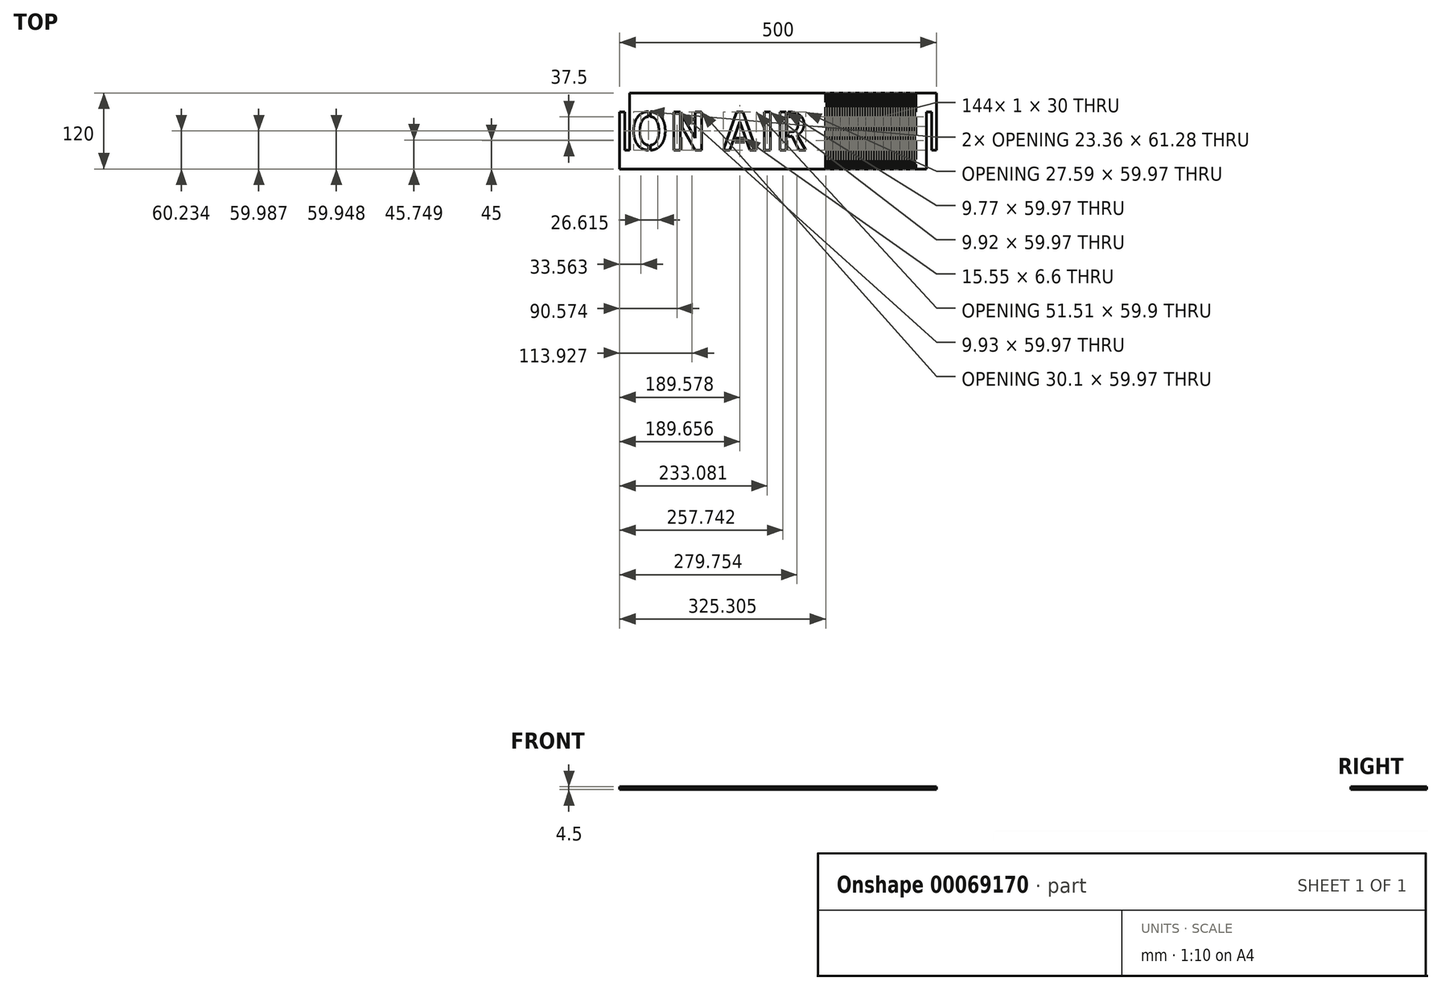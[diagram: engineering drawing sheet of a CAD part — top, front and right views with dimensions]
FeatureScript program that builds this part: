
annotation { "Feature Type Name" : "Feature", "Feature Type Description" : "" }
export const myFeature = defineFeature(function(context is Context, id is Id, definition is map)
    precondition{}
    {
        {
            var Q0;
            Q0=qCreatedBy(makeId("Top.planeOp"),FACE);
            var sketch = newSketch(context, id + "F0", { "sketchPlane" : qUnion([Q0])});
            skLineSegment(sketch, "E0", {"start": v(0, 0) * mm, "end": v(484.38, 0) * mm});
            skLineSegment(sketch, "E1", {"start": v(484.38, 0) * mm, "end": v(484.38, 90) * mm});
            skLineSegment(sketch, "E2", {"start": v(484.38, 90) * mm, "end": v(492.19, 90) * mm});
            skLineSegment(sketch, "E3", {"start": v(492.19, 90) * mm, "end": v(492.19, 30) * mm});
            skLineSegment(sketch, "E4", {"start": v(500, 30) * mm, "end": v(500, 120) * mm});
            skLineSegment(sketch, "E5", {"start": v(500, 120) * mm, "end": v(15.62, 120) * mm});
            skLineSegment(sketch, "E6", {"start": v(0, 90) * mm, "end": v(0, 0) * mm});
            skText(sketch, "E7", { "text": "ON AIR", "fontName": "AllertaStencil-Regular.ttf"});
            skLineSegment(sketch, "E8", {"start": v(7.81, 90) * mm, "end": v(7.81, 30) * mm});
            skLineSegment(sketch, "E9", {"start": v(7.81, 30) * mm, "end": v(15.62, 30) * mm});
            skLineSegment(sketch, "E10", {"start": v(15.62, 30) * mm, "end": v(15.62, 120) * mm});
            skLineSegment(sketch, "E11", {"start": v(0, 90) * mm, "end": v(7.81, 90) * mm});
            skLineSegment(sketch, "E12", {"start": v(492.19, 30) * mm, "end": v(500, 30) * mm});
            skLineSegment(sketch, "E13", {"start": v(324.8, 135) * mm, "end": v(324.8, 105) * mm});
            skLineSegment(sketch, "E14", {"start": v(324.8, 105) * mm, "end": v(325.8, 105) * mm});
            skLineSegment(sketch, "E15", {"start": v(325.8, 105) * mm, "end": v(325.8, 135) * mm});
            skLineSegment(sketch, "E16", {"start": v(325.8, 135) * mm, "end": v(324.8, 135) * mm});
            skPoint(sketch, "E17", {"position": v(324.8, 120) * mm});
            skLineSegment(sketch, "E18", {"start": v(326.8, 120) * mm, "end": v(326.8, 90) * mm});
            skLineSegment(sketch, "E19", {"start": v(326.8, 90) * mm, "end": v(327.8, 90) * mm});
            skLineSegment(sketch, "E20", {"start": v(327.8, 90) * mm, "end": v(327.8, 120) * mm});
            skLineSegment(sketch, "E21", {"start": v(327.8, 120) * mm, "end": v(326.8, 120) * mm});
            skLineSegment(sketch, "E22.0.1.0", {"start": v(327.8, 52.5) * mm, "end": v(327.8, 82.5) * mm});
            skLineSegment(sketch, "E22.0.1.1", {"start": v(324.8, 97.5) * mm, "end": v(324.8, 67.5) * mm});
            skPoint(sketch, "E22.0.1.2", {"position": v(324.8, 82.5) * mm});
            skLineSegment(sketch, "E22.0.1.3", {"start": v(325.8, 67.5) * mm, "end": v(325.8, 97.5) * mm});
            skLineSegment(sketch, "E22.0.1.4", {"start": v(326.8, 82.5) * mm, "end": v(326.8, 52.5) * mm});
            skLineSegment(sketch, "E22.0.1.5", {"start": v(324.8, 67.5) * mm, "end": v(325.8, 67.5) * mm});
            skLineSegment(sketch, "E22.0.1.6", {"start": v(327.8, 82.5) * mm, "end": v(326.8, 82.5) * mm});
            skLineSegment(sketch, "E22.0.1.7", {"start": v(325.8, 97.5) * mm, "end": v(324.8, 97.5) * mm});
            skLineSegment(sketch, "E22.0.1.8", {"start": v(326.8, 52.5) * mm, "end": v(327.8, 52.5) * mm});
            skLineSegment(sketch, "E22.0.2.0", {"start": v(327.8, 15) * mm, "end": v(327.8, 45) * mm});
            skLineSegment(sketch, "E22.0.2.1", {"start": v(324.8, 60) * mm, "end": v(324.8, 30) * mm});
            skPoint(sketch, "E22.0.2.2", {"position": v(324.8, 45) * mm});
            skLineSegment(sketch, "E22.0.2.3", {"start": v(325.8, 30) * mm, "end": v(325.8, 60) * mm});
            skLineSegment(sketch, "E22.0.2.4", {"start": v(326.8, 45) * mm, "end": v(326.8, 15) * mm});
            skLineSegment(sketch, "E22.0.2.5", {"start": v(324.8, 30) * mm, "end": v(325.8, 30) * mm});
            skLineSegment(sketch, "E22.0.2.6", {"start": v(327.8, 45) * mm, "end": v(326.8, 45) * mm});
            skLineSegment(sketch, "E22.0.2.7", {"start": v(325.8, 60) * mm, "end": v(324.8, 60) * mm});
            skLineSegment(sketch, "E22.0.2.8", {"start": v(326.8, 15) * mm, "end": v(327.8, 15) * mm});
            skLineSegment(sketch, "E22.0.3.0", {"start": v(327.8, -22.5) * mm, "end": v(327.8, 7.5) * mm});
            skLineSegment(sketch, "E22.0.3.1", {"start": v(324.8, 22.5) * mm, "end": v(324.8, -7.5) * mm});
            skPoint(sketch, "E22.0.3.2", {"position": v(324.8, 7.5) * mm});
            skLineSegment(sketch, "E22.0.3.3", {"start": v(325.8, -7.5) * mm, "end": v(325.8, 22.5) * mm});
            skLineSegment(sketch, "E22.0.3.4", {"start": v(326.8, 7.5) * mm, "end": v(326.8, -22.5) * mm});
            skLineSegment(sketch, "E22.0.3.5", {"start": v(324.8, -7.5) * mm, "end": v(325.8, -7.5) * mm});
            skLineSegment(sketch, "E22.0.3.6", {"start": v(327.8, 7.5) * mm, "end": v(326.8, 7.5) * mm});
            skLineSegment(sketch, "E22.0.3.7", {"start": v(325.8, 22.5) * mm, "end": v(324.8, 22.5) * mm});
            skLineSegment(sketch, "E22.0.3.8", {"start": v(326.8, -22.5) * mm, "end": v(327.8, -22.5) * mm});
            skLineSegment(sketch, "E22.1.0.0", {"start": v(331.8, 90) * mm, "end": v(331.8, 120) * mm});
            skLineSegment(sketch, "E22.1.0.1", {"start": v(328.8, 135) * mm, "end": v(328.8, 105) * mm});
            skPoint(sketch, "E22.1.0.2", {"position": v(328.8, 120) * mm});
            skLineSegment(sketch, "E22.1.0.3", {"start": v(329.8, 105) * mm, "end": v(329.8, 135) * mm});
            skLineSegment(sketch, "E22.1.0.4", {"start": v(330.8, 120) * mm, "end": v(330.8, 90) * mm});
            skLineSegment(sketch, "E22.1.0.5", {"start": v(328.8, 105) * mm, "end": v(329.8, 105) * mm});
            skLineSegment(sketch, "E22.1.0.6", {"start": v(331.8, 120) * mm, "end": v(330.8, 120) * mm});
            skLineSegment(sketch, "E22.1.0.7", {"start": v(329.8, 135) * mm, "end": v(328.8, 135) * mm});
            skLineSegment(sketch, "E22.1.0.8", {"start": v(330.8, 90) * mm, "end": v(331.8, 90) * mm});
            skLineSegment(sketch, "E22.1.1.0", {"start": v(331.8, 52.5) * mm, "end": v(331.8, 82.5) * mm});
            skLineSegment(sketch, "E22.1.1.1", {"start": v(328.8, 97.5) * mm, "end": v(328.8, 67.5) * mm});
            skPoint(sketch, "E22.1.1.2", {"position": v(328.8, 82.5) * mm});
            skLineSegment(sketch, "E22.1.1.3", {"start": v(329.8, 67.5) * mm, "end": v(329.8, 97.5) * mm});
            skLineSegment(sketch, "E22.1.1.4", {"start": v(330.8, 82.5) * mm, "end": v(330.8, 52.5) * mm});
            skLineSegment(sketch, "E22.1.1.5", {"start": v(328.8, 67.5) * mm, "end": v(329.8, 67.5) * mm});
            skLineSegment(sketch, "E22.1.1.6", {"start": v(331.8, 82.5) * mm, "end": v(330.8, 82.5) * mm});
            skLineSegment(sketch, "E22.1.1.7", {"start": v(329.8, 97.5) * mm, "end": v(328.8, 97.5) * mm});
            skLineSegment(sketch, "E22.1.1.8", {"start": v(330.8, 52.5) * mm, "end": v(331.8, 52.5) * mm});
            skLineSegment(sketch, "E22.1.2.0", {"start": v(331.8, 15) * mm, "end": v(331.8, 45) * mm});
            skLineSegment(sketch, "E22.1.2.1", {"start": v(328.8, 60) * mm, "end": v(328.8, 30) * mm});
            skPoint(sketch, "E22.1.2.2", {"position": v(328.8, 45) * mm});
            skLineSegment(sketch, "E22.1.2.3", {"start": v(329.8, 30) * mm, "end": v(329.8, 60) * mm});
            skLineSegment(sketch, "E22.1.2.4", {"start": v(330.8, 45) * mm, "end": v(330.8, 15) * mm});
            skLineSegment(sketch, "E22.1.2.5", {"start": v(328.8, 30) * mm, "end": v(329.8, 30) * mm});
            skLineSegment(sketch, "E22.1.2.6", {"start": v(331.8, 45) * mm, "end": v(330.8, 45) * mm});
            skLineSegment(sketch, "E22.1.2.7", {"start": v(329.8, 60) * mm, "end": v(328.8, 60) * mm});
            skLineSegment(sketch, "E22.1.2.8", {"start": v(330.8, 15) * mm, "end": v(331.8, 15) * mm});
            skLineSegment(sketch, "E22.1.3.0", {"start": v(331.8, -22.5) * mm, "end": v(331.8, 7.5) * mm});
            skLineSegment(sketch, "E22.1.3.1", {"start": v(328.8, 22.5) * mm, "end": v(328.8, -7.5) * mm});
            skPoint(sketch, "E22.1.3.2", {"position": v(328.8, 7.5) * mm});
            skLineSegment(sketch, "E22.1.3.3", {"start": v(329.8, -7.5) * mm, "end": v(329.8, 22.5) * mm});
            skLineSegment(sketch, "E22.1.3.4", {"start": v(330.8, 7.5) * mm, "end": v(330.8, -22.5) * mm});
            skLineSegment(sketch, "E22.1.3.5", {"start": v(328.8, -7.5) * mm, "end": v(329.8, -7.5) * mm});
            skLineSegment(sketch, "E22.1.3.6", {"start": v(331.8, 7.5) * mm, "end": v(330.8, 7.5) * mm});
            skLineSegment(sketch, "E22.1.3.7", {"start": v(329.8, 22.5) * mm, "end": v(328.8, 22.5) * mm});
            skLineSegment(sketch, "E22.1.3.8", {"start": v(330.8, -22.5) * mm, "end": v(331.8, -22.5) * mm});
            skLineSegment(sketch, "E22.2.0.0", {"start": v(335.8, 90) * mm, "end": v(335.8, 120) * mm});
            skLineSegment(sketch, "E22.2.0.1", {"start": v(332.8, 135) * mm, "end": v(332.8, 105) * mm});
            skPoint(sketch, "E22.2.0.2", {"position": v(332.8, 120) * mm});
            skLineSegment(sketch, "E22.2.0.3", {"start": v(333.8, 105) * mm, "end": v(333.8, 135) * mm});
            skLineSegment(sketch, "E22.2.0.4", {"start": v(334.8, 120) * mm, "end": v(334.8, 90) * mm});
            skLineSegment(sketch, "E22.2.0.5", {"start": v(332.8, 105) * mm, "end": v(333.8, 105) * mm});
            skLineSegment(sketch, "E22.2.0.6", {"start": v(335.8, 120) * mm, "end": v(334.8, 120) * mm});
            skLineSegment(sketch, "E22.2.0.7", {"start": v(333.8, 135) * mm, "end": v(332.8, 135) * mm});
            skLineSegment(sketch, "E22.2.0.8", {"start": v(334.8, 90) * mm, "end": v(335.8, 90) * mm});
            skLineSegment(sketch, "E22.2.1.0", {"start": v(335.8, 52.5) * mm, "end": v(335.8, 82.5) * mm});
            skLineSegment(sketch, "E22.2.1.1", {"start": v(332.8, 97.5) * mm, "end": v(332.8, 67.5) * mm});
            skPoint(sketch, "E22.2.1.2", {"position": v(332.8, 82.5) * mm});
            skLineSegment(sketch, "E22.2.1.3", {"start": v(333.8, 67.5) * mm, "end": v(333.8, 97.5) * mm});
            skLineSegment(sketch, "E22.2.1.4", {"start": v(334.8, 82.5) * mm, "end": v(334.8, 52.5) * mm});
            skLineSegment(sketch, "E22.2.1.5", {"start": v(332.8, 67.5) * mm, "end": v(333.8, 67.5) * mm});
            skLineSegment(sketch, "E22.2.1.6", {"start": v(335.8, 82.5) * mm, "end": v(334.8, 82.5) * mm});
            skLineSegment(sketch, "E22.2.1.7", {"start": v(333.8, 97.5) * mm, "end": v(332.8, 97.5) * mm});
            skLineSegment(sketch, "E22.2.1.8", {"start": v(334.8, 52.5) * mm, "end": v(335.8, 52.5) * mm});
            skLineSegment(sketch, "E22.2.2.0", {"start": v(335.8, 15) * mm, "end": v(335.8, 45) * mm});
            skLineSegment(sketch, "E22.2.2.1", {"start": v(332.8, 60) * mm, "end": v(332.8, 30) * mm});
            skPoint(sketch, "E22.2.2.2", {"position": v(332.8, 45) * mm});
            skLineSegment(sketch, "E22.2.2.3", {"start": v(333.8, 30) * mm, "end": v(333.8, 60) * mm});
            skLineSegment(sketch, "E22.2.2.4", {"start": v(334.8, 45) * mm, "end": v(334.8, 15) * mm});
            skLineSegment(sketch, "E22.2.2.5", {"start": v(332.8, 30) * mm, "end": v(333.8, 30) * mm});
            skLineSegment(sketch, "E22.2.2.6", {"start": v(335.8, 45) * mm, "end": v(334.8, 45) * mm});
            skLineSegment(sketch, "E22.2.2.7", {"start": v(333.8, 60) * mm, "end": v(332.8, 60) * mm});
            skLineSegment(sketch, "E22.2.2.8", {"start": v(334.8, 15) * mm, "end": v(335.8, 15) * mm});
            skLineSegment(sketch, "E22.2.3.0", {"start": v(335.8, -22.5) * mm, "end": v(335.8, 7.5) * mm});
            skLineSegment(sketch, "E22.2.3.1", {"start": v(332.8, 22.5) * mm, "end": v(332.8, -7.5) * mm});
            skPoint(sketch, "E22.2.3.2", {"position": v(332.8, 7.5) * mm});
            skLineSegment(sketch, "E22.2.3.3", {"start": v(333.8, -7.5) * mm, "end": v(333.8, 22.5) * mm});
            skLineSegment(sketch, "E22.2.3.4", {"start": v(334.8, 7.5) * mm, "end": v(334.8, -22.5) * mm});
            skLineSegment(sketch, "E22.2.3.5", {"start": v(332.8, -7.5) * mm, "end": v(333.8, -7.5) * mm});
            skLineSegment(sketch, "E22.2.3.6", {"start": v(335.8, 7.5) * mm, "end": v(334.8, 7.5) * mm});
            skLineSegment(sketch, "E22.2.3.7", {"start": v(333.8, 22.5) * mm, "end": v(332.8, 22.5) * mm});
            skLineSegment(sketch, "E22.2.3.8", {"start": v(334.8, -22.5) * mm, "end": v(335.8, -22.5) * mm});
            skLineSegment(sketch, "E22.3.0.0", {"start": v(339.8, 90) * mm, "end": v(339.8, 120) * mm});
            skLineSegment(sketch, "E22.3.0.1", {"start": v(336.8, 135) * mm, "end": v(336.8, 105) * mm});
            skPoint(sketch, "E22.3.0.2", {"position": v(336.8, 120) * mm});
            skLineSegment(sketch, "E22.3.0.3", {"start": v(337.8, 105) * mm, "end": v(337.8, 135) * mm});
            skLineSegment(sketch, "E22.3.0.4", {"start": v(338.8, 120) * mm, "end": v(338.8, 90) * mm});
            skLineSegment(sketch, "E22.3.0.5", {"start": v(336.8, 105) * mm, "end": v(337.8, 105) * mm});
            skLineSegment(sketch, "E22.3.0.6", {"start": v(339.8, 120) * mm, "end": v(338.8, 120) * mm});
            skLineSegment(sketch, "E22.3.0.7", {"start": v(337.8, 135) * mm, "end": v(336.8, 135) * mm});
            skLineSegment(sketch, "E22.3.0.8", {"start": v(338.8, 90) * mm, "end": v(339.8, 90) * mm});
            skLineSegment(sketch, "E22.3.1.0", {"start": v(339.8, 52.5) * mm, "end": v(339.8, 82.5) * mm});
            skLineSegment(sketch, "E22.3.1.1", {"start": v(336.8, 97.5) * mm, "end": v(336.8, 67.5) * mm});
            skPoint(sketch, "E22.3.1.2", {"position": v(336.8, 82.5) * mm});
            skLineSegment(sketch, "E22.3.1.3", {"start": v(337.8, 67.5) * mm, "end": v(337.8, 97.5) * mm});
            skLineSegment(sketch, "E22.3.1.4", {"start": v(338.8, 82.5) * mm, "end": v(338.8, 52.5) * mm});
            skLineSegment(sketch, "E22.3.1.5", {"start": v(336.8, 67.5) * mm, "end": v(337.8, 67.5) * mm});
            skLineSegment(sketch, "E22.3.1.6", {"start": v(339.8, 82.5) * mm, "end": v(338.8, 82.5) * mm});
            skLineSegment(sketch, "E22.3.1.7", {"start": v(337.8, 97.5) * mm, "end": v(336.8, 97.5) * mm});
            skLineSegment(sketch, "E22.3.1.8", {"start": v(338.8, 52.5) * mm, "end": v(339.8, 52.5) * mm});
            skLineSegment(sketch, "E22.3.2.0", {"start": v(339.8, 15) * mm, "end": v(339.8, 45) * mm});
            skLineSegment(sketch, "E22.3.2.1", {"start": v(336.8, 60) * mm, "end": v(336.8, 30) * mm});
            skPoint(sketch, "E22.3.2.2", {"position": v(336.8, 45) * mm});
            skLineSegment(sketch, "E22.3.2.3", {"start": v(337.8, 30) * mm, "end": v(337.8, 60) * mm});
            skLineSegment(sketch, "E22.3.2.4", {"start": v(338.8, 45) * mm, "end": v(338.8, 15) * mm});
            skLineSegment(sketch, "E22.3.2.5", {"start": v(336.8, 30) * mm, "end": v(337.8, 30) * mm});
            skLineSegment(sketch, "E22.3.2.6", {"start": v(339.8, 45) * mm, "end": v(338.8, 45) * mm});
            skLineSegment(sketch, "E22.3.2.7", {"start": v(337.8, 60) * mm, "end": v(336.8, 60) * mm});
            skLineSegment(sketch, "E22.3.2.8", {"start": v(338.8, 15) * mm, "end": v(339.8, 15) * mm});
            skLineSegment(sketch, "E22.3.3.0", {"start": v(339.8, -22.5) * mm, "end": v(339.8, 7.5) * mm});
            skLineSegment(sketch, "E22.3.3.1", {"start": v(336.8, 22.5) * mm, "end": v(336.8, -7.5) * mm});
            skPoint(sketch, "E22.3.3.2", {"position": v(336.8, 7.5) * mm});
            skLineSegment(sketch, "E22.3.3.3", {"start": v(337.8, -7.5) * mm, "end": v(337.8, 22.5) * mm});
            skLineSegment(sketch, "E22.3.3.4", {"start": v(338.8, 7.5) * mm, "end": v(338.8, -22.5) * mm});
            skLineSegment(sketch, "E22.3.3.5", {"start": v(336.8, -7.5) * mm, "end": v(337.8, -7.5) * mm});
            skLineSegment(sketch, "E22.3.3.6", {"start": v(339.8, 7.5) * mm, "end": v(338.8, 7.5) * mm});
            skLineSegment(sketch, "E22.3.3.7", {"start": v(337.8, 22.5) * mm, "end": v(336.8, 22.5) * mm});
            skLineSegment(sketch, "E22.3.3.8", {"start": v(338.8, -22.5) * mm, "end": v(339.8, -22.5) * mm});
            skLineSegment(sketch, "E22.4.0.0", {"start": v(343.8, 90) * mm, "end": v(343.8, 120) * mm});
            skLineSegment(sketch, "E22.4.0.1", {"start": v(340.8, 135) * mm, "end": v(340.8, 105) * mm});
            skPoint(sketch, "E22.4.0.2", {"position": v(340.8, 120) * mm});
            skLineSegment(sketch, "E22.4.0.3", {"start": v(341.8, 105) * mm, "end": v(341.8, 135) * mm});
            skLineSegment(sketch, "E22.4.0.4", {"start": v(342.8, 120) * mm, "end": v(342.8, 90) * mm});
            skLineSegment(sketch, "E22.4.0.5", {"start": v(340.8, 105) * mm, "end": v(341.8, 105) * mm});
            skLineSegment(sketch, "E22.4.0.6", {"start": v(343.8, 120) * mm, "end": v(342.8, 120) * mm});
            skLineSegment(sketch, "E22.4.0.7", {"start": v(341.8, 135) * mm, "end": v(340.8, 135) * mm});
            skLineSegment(sketch, "E22.4.0.8", {"start": v(342.8, 90) * mm, "end": v(343.8, 90) * mm});
            skLineSegment(sketch, "E22.4.1.0", {"start": v(343.8, 52.5) * mm, "end": v(343.8, 82.5) * mm});
            skLineSegment(sketch, "E22.4.1.1", {"start": v(340.8, 97.5) * mm, "end": v(340.8, 67.5) * mm});
            skPoint(sketch, "E22.4.1.2", {"position": v(340.8, 82.5) * mm});
            skLineSegment(sketch, "E22.4.1.3", {"start": v(341.8, 67.5) * mm, "end": v(341.8, 97.5) * mm});
            skLineSegment(sketch, "E22.4.1.4", {"start": v(342.8, 82.5) * mm, "end": v(342.8, 52.5) * mm});
            skLineSegment(sketch, "E22.4.1.5", {"start": v(340.8, 67.5) * mm, "end": v(341.8, 67.5) * mm});
            skLineSegment(sketch, "E22.4.1.6", {"start": v(343.8, 82.5) * mm, "end": v(342.8, 82.5) * mm});
            skLineSegment(sketch, "E22.4.1.7", {"start": v(341.8, 97.5) * mm, "end": v(340.8, 97.5) * mm});
            skLineSegment(sketch, "E22.4.1.8", {"start": v(342.8, 52.5) * mm, "end": v(343.8, 52.5) * mm});
            skLineSegment(sketch, "E22.4.2.0", {"start": v(343.8, 15) * mm, "end": v(343.8, 45) * mm});
            skLineSegment(sketch, "E22.4.2.1", {"start": v(340.8, 60) * mm, "end": v(340.8, 30) * mm});
            skPoint(sketch, "E22.4.2.2", {"position": v(340.8, 45) * mm});
            skLineSegment(sketch, "E22.4.2.3", {"start": v(341.8, 30) * mm, "end": v(341.8, 60) * mm});
            skLineSegment(sketch, "E22.4.2.4", {"start": v(342.8, 45) * mm, "end": v(342.8, 15) * mm});
            skLineSegment(sketch, "E22.4.2.5", {"start": v(340.8, 30) * mm, "end": v(341.8, 30) * mm});
            skLineSegment(sketch, "E22.4.2.6", {"start": v(343.8, 45) * mm, "end": v(342.8, 45) * mm});
            skLineSegment(sketch, "E22.4.2.7", {"start": v(341.8, 60) * mm, "end": v(340.8, 60) * mm});
            skLineSegment(sketch, "E22.4.2.8", {"start": v(342.8, 15) * mm, "end": v(343.8, 15) * mm});
            skLineSegment(sketch, "E22.4.3.0", {"start": v(343.8, -22.5) * mm, "end": v(343.8, 7.5) * mm});
            skLineSegment(sketch, "E22.4.3.1", {"start": v(340.8, 22.5) * mm, "end": v(340.8, -7.5) * mm});
            skPoint(sketch, "E22.4.3.2", {"position": v(340.8, 7.5) * mm});
            skLineSegment(sketch, "E22.4.3.3", {"start": v(341.8, -7.5) * mm, "end": v(341.8, 22.5) * mm});
            skLineSegment(sketch, "E22.4.3.4", {"start": v(342.8, 7.5) * mm, "end": v(342.8, -22.5) * mm});
            skLineSegment(sketch, "E22.4.3.5", {"start": v(340.8, -7.5) * mm, "end": v(341.8, -7.5) * mm});
            skLineSegment(sketch, "E22.4.3.6", {"start": v(343.8, 7.5) * mm, "end": v(342.8, 7.5) * mm});
            skLineSegment(sketch, "E22.4.3.7", {"start": v(341.8, 22.5) * mm, "end": v(340.8, 22.5) * mm});
            skLineSegment(sketch, "E22.4.3.8", {"start": v(342.8, -22.5) * mm, "end": v(343.8, -22.5) * mm});
            skLineSegment(sketch, "E22.5.0.0", {"start": v(347.8, 90) * mm, "end": v(347.8, 120) * mm});
            skLineSegment(sketch, "E22.5.0.1", {"start": v(344.8, 135) * mm, "end": v(344.8, 105) * mm});
            skPoint(sketch, "E22.5.0.2", {"position": v(344.8, 120) * mm});
            skLineSegment(sketch, "E22.5.0.3", {"start": v(345.8, 105) * mm, "end": v(345.8, 135) * mm});
            skLineSegment(sketch, "E22.5.0.4", {"start": v(346.8, 120) * mm, "end": v(346.8, 90) * mm});
            skLineSegment(sketch, "E22.5.0.5", {"start": v(344.8, 105) * mm, "end": v(345.8, 105) * mm});
            skLineSegment(sketch, "E22.5.0.6", {"start": v(347.8, 120) * mm, "end": v(346.8, 120) * mm});
            skLineSegment(sketch, "E22.5.0.7", {"start": v(345.8, 135) * mm, "end": v(344.8, 135) * mm});
            skLineSegment(sketch, "E22.5.0.8", {"start": v(346.8, 90) * mm, "end": v(347.8, 90) * mm});
            skLineSegment(sketch, "E22.5.1.0", {"start": v(347.8, 52.5) * mm, "end": v(347.8, 82.5) * mm});
            skLineSegment(sketch, "E22.5.1.1", {"start": v(344.8, 97.5) * mm, "end": v(344.8, 67.5) * mm});
            skPoint(sketch, "E22.5.1.2", {"position": v(344.8, 82.5) * mm});
            skLineSegment(sketch, "E22.5.1.3", {"start": v(345.8, 67.5) * mm, "end": v(345.8, 97.5) * mm});
            skLineSegment(sketch, "E22.5.1.4", {"start": v(346.8, 82.5) * mm, "end": v(346.8, 52.5) * mm});
            skLineSegment(sketch, "E22.5.1.5", {"start": v(344.8, 67.5) * mm, "end": v(345.8, 67.5) * mm});
            skLineSegment(sketch, "E22.5.1.6", {"start": v(347.8, 82.5) * mm, "end": v(346.8, 82.5) * mm});
            skLineSegment(sketch, "E22.5.1.7", {"start": v(345.8, 97.5) * mm, "end": v(344.8, 97.5) * mm});
            skLineSegment(sketch, "E22.5.1.8", {"start": v(346.8, 52.5) * mm, "end": v(347.8, 52.5) * mm});
            skLineSegment(sketch, "E22.5.2.0", {"start": v(347.8, 15) * mm, "end": v(347.8, 45) * mm});
            skLineSegment(sketch, "E22.5.2.1", {"start": v(344.8, 60) * mm, "end": v(344.8, 30) * mm});
            skPoint(sketch, "E22.5.2.2", {"position": v(344.8, 45) * mm});
            skLineSegment(sketch, "E22.5.2.3", {"start": v(345.8, 30) * mm, "end": v(345.8, 60) * mm});
            skLineSegment(sketch, "E22.5.2.4", {"start": v(346.8, 45) * mm, "end": v(346.8, 15) * mm});
            skLineSegment(sketch, "E22.5.2.5", {"start": v(344.8, 30) * mm, "end": v(345.8, 30) * mm});
            skLineSegment(sketch, "E22.5.2.6", {"start": v(347.8, 45) * mm, "end": v(346.8, 45) * mm});
            skLineSegment(sketch, "E22.5.2.7", {"start": v(345.8, 60) * mm, "end": v(344.8, 60) * mm});
            skLineSegment(sketch, "E22.5.2.8", {"start": v(346.8, 15) * mm, "end": v(347.8, 15) * mm});
            skLineSegment(sketch, "E22.5.3.0", {"start": v(347.8, -22.5) * mm, "end": v(347.8, 7.5) * mm});
            skLineSegment(sketch, "E22.5.3.1", {"start": v(344.8, 22.5) * mm, "end": v(344.8, -7.5) * mm});
            skPoint(sketch, "E22.5.3.2", {"position": v(344.8, 7.5) * mm});
            skLineSegment(sketch, "E22.5.3.3", {"start": v(345.8, -7.5) * mm, "end": v(345.8, 22.5) * mm});
            skLineSegment(sketch, "E22.5.3.4", {"start": v(346.8, 7.5) * mm, "end": v(346.8, -22.5) * mm});
            skLineSegment(sketch, "E22.5.3.5", {"start": v(344.8, -7.5) * mm, "end": v(345.8, -7.5) * mm});
            skLineSegment(sketch, "E22.5.3.6", {"start": v(347.8, 7.5) * mm, "end": v(346.8, 7.5) * mm});
            skLineSegment(sketch, "E22.5.3.7", {"start": v(345.8, 22.5) * mm, "end": v(344.8, 22.5) * mm});
            skLineSegment(sketch, "E22.5.3.8", {"start": v(346.8, -22.5) * mm, "end": v(347.8, -22.5) * mm});
            skLineSegment(sketch, "E22.6.0.0", {"start": v(351.8, 90) * mm, "end": v(351.8, 120) * mm});
            skLineSegment(sketch, "E22.6.0.1", {"start": v(348.8, 135) * mm, "end": v(348.8, 105) * mm});
            skPoint(sketch, "E22.6.0.2", {"position": v(348.8, 120) * mm});
            skLineSegment(sketch, "E22.6.0.3", {"start": v(349.8, 105) * mm, "end": v(349.8, 135) * mm});
            skLineSegment(sketch, "E22.6.0.4", {"start": v(350.8, 120) * mm, "end": v(350.8, 90) * mm});
            skLineSegment(sketch, "E22.6.0.5", {"start": v(348.8, 105) * mm, "end": v(349.8, 105) * mm});
            skLineSegment(sketch, "E22.6.0.6", {"start": v(351.8, 120) * mm, "end": v(350.8, 120) * mm});
            skLineSegment(sketch, "E22.6.0.7", {"start": v(349.8, 135) * mm, "end": v(348.8, 135) * mm});
            skLineSegment(sketch, "E22.6.0.8", {"start": v(350.8, 90) * mm, "end": v(351.8, 90) * mm});
            skLineSegment(sketch, "E22.6.1.0", {"start": v(351.8, 52.5) * mm, "end": v(351.8, 82.5) * mm});
            skLineSegment(sketch, "E22.6.1.1", {"start": v(348.8, 97.5) * mm, "end": v(348.8, 67.5) * mm});
            skPoint(sketch, "E22.6.1.2", {"position": v(348.8, 82.5) * mm});
            skLineSegment(sketch, "E22.6.1.3", {"start": v(349.8, 67.5) * mm, "end": v(349.8, 97.5) * mm});
            skLineSegment(sketch, "E22.6.1.4", {"start": v(350.8, 82.5) * mm, "end": v(350.8, 52.5) * mm});
            skLineSegment(sketch, "E22.6.1.5", {"start": v(348.8, 67.5) * mm, "end": v(349.8, 67.5) * mm});
            skLineSegment(sketch, "E22.6.1.6", {"start": v(351.8, 82.5) * mm, "end": v(350.8, 82.5) * mm});
            skLineSegment(sketch, "E22.6.1.7", {"start": v(349.8, 97.5) * mm, "end": v(348.8, 97.5) * mm});
            skLineSegment(sketch, "E22.6.1.8", {"start": v(350.8, 52.5) * mm, "end": v(351.8, 52.5) * mm});
            skLineSegment(sketch, "E22.6.2.0", {"start": v(351.8, 15) * mm, "end": v(351.8, 45) * mm});
            skLineSegment(sketch, "E22.6.2.1", {"start": v(348.8, 60) * mm, "end": v(348.8, 30) * mm});
            skPoint(sketch, "E22.6.2.2", {"position": v(348.8, 45) * mm});
            skLineSegment(sketch, "E22.6.2.3", {"start": v(349.8, 30) * mm, "end": v(349.8, 60) * mm});
            skLineSegment(sketch, "E22.6.2.4", {"start": v(350.8, 45) * mm, "end": v(350.8, 15) * mm});
            skLineSegment(sketch, "E22.6.2.5", {"start": v(348.8, 30) * mm, "end": v(349.8, 30) * mm});
            skLineSegment(sketch, "E22.6.2.6", {"start": v(351.8, 45) * mm, "end": v(350.8, 45) * mm});
            skLineSegment(sketch, "E22.6.2.7", {"start": v(349.8, 60) * mm, "end": v(348.8, 60) * mm});
            skLineSegment(sketch, "E22.6.2.8", {"start": v(350.8, 15) * mm, "end": v(351.8, 15) * mm});
            skLineSegment(sketch, "E22.6.3.0", {"start": v(351.8, -22.5) * mm, "end": v(351.8, 7.5) * mm});
            skLineSegment(sketch, "E22.6.3.1", {"start": v(348.8, 22.5) * mm, "end": v(348.8, -7.5) * mm});
            skPoint(sketch, "E22.6.3.2", {"position": v(348.8, 7.5) * mm});
            skLineSegment(sketch, "E22.6.3.3", {"start": v(349.8, -7.5) * mm, "end": v(349.8, 22.5) * mm});
            skLineSegment(sketch, "E22.6.3.4", {"start": v(350.8, 7.5) * mm, "end": v(350.8, -22.5) * mm});
            skLineSegment(sketch, "E22.6.3.5", {"start": v(348.8, -7.5) * mm, "end": v(349.8, -7.5) * mm});
            skLineSegment(sketch, "E22.6.3.6", {"start": v(351.8, 7.5) * mm, "end": v(350.8, 7.5) * mm});
            skLineSegment(sketch, "E22.6.3.7", {"start": v(349.8, 22.5) * mm, "end": v(348.8, 22.5) * mm});
            skLineSegment(sketch, "E22.6.3.8", {"start": v(350.8, -22.5) * mm, "end": v(351.8, -22.5) * mm});
            skLineSegment(sketch, "E22.7.0.0", {"start": v(355.8, 90) * mm, "end": v(355.8, 120) * mm});
            skLineSegment(sketch, "E22.7.0.1", {"start": v(352.8, 135) * mm, "end": v(352.8, 105) * mm});
            skPoint(sketch, "E22.7.0.2", {"position": v(352.8, 120) * mm});
            skLineSegment(sketch, "E22.7.0.3", {"start": v(353.8, 105) * mm, "end": v(353.8, 135) * mm});
            skLineSegment(sketch, "E22.7.0.4", {"start": v(354.8, 120) * mm, "end": v(354.8, 90) * mm});
            skLineSegment(sketch, "E22.7.0.5", {"start": v(352.8, 105) * mm, "end": v(353.8, 105) * mm});
            skLineSegment(sketch, "E22.7.0.6", {"start": v(355.8, 120) * mm, "end": v(354.8, 120) * mm});
            skLineSegment(sketch, "E22.7.0.7", {"start": v(353.8, 135) * mm, "end": v(352.8, 135) * mm});
            skLineSegment(sketch, "E22.7.0.8", {"start": v(354.8, 90) * mm, "end": v(355.8, 90) * mm});
            skLineSegment(sketch, "E22.7.1.0", {"start": v(355.8, 52.5) * mm, "end": v(355.8, 82.5) * mm});
            skLineSegment(sketch, "E22.7.1.1", {"start": v(352.8, 97.5) * mm, "end": v(352.8, 67.5) * mm});
            skPoint(sketch, "E22.7.1.2", {"position": v(352.8, 82.5) * mm});
            skLineSegment(sketch, "E22.7.1.3", {"start": v(353.8, 67.5) * mm, "end": v(353.8, 97.5) * mm});
            skLineSegment(sketch, "E22.7.1.4", {"start": v(354.8, 82.5) * mm, "end": v(354.8, 52.5) * mm});
            skLineSegment(sketch, "E22.7.1.5", {"start": v(352.8, 67.5) * mm, "end": v(353.8, 67.5) * mm});
            skLineSegment(sketch, "E22.7.1.6", {"start": v(355.8, 82.5) * mm, "end": v(354.8, 82.5) * mm});
            skLineSegment(sketch, "E22.7.1.7", {"start": v(353.8, 97.5) * mm, "end": v(352.8, 97.5) * mm});
            skLineSegment(sketch, "E22.7.1.8", {"start": v(354.8, 52.5) * mm, "end": v(355.8, 52.5) * mm});
            skLineSegment(sketch, "E22.7.2.0", {"start": v(355.8, 15) * mm, "end": v(355.8, 45) * mm});
            skLineSegment(sketch, "E22.7.2.1", {"start": v(352.8, 60) * mm, "end": v(352.8, 30) * mm});
            skPoint(sketch, "E22.7.2.2", {"position": v(352.8, 45) * mm});
            skLineSegment(sketch, "E22.7.2.3", {"start": v(353.8, 30) * mm, "end": v(353.8, 60) * mm});
            skLineSegment(sketch, "E22.7.2.4", {"start": v(354.8, 45) * mm, "end": v(354.8, 15) * mm});
            skLineSegment(sketch, "E22.7.2.5", {"start": v(352.8, 30) * mm, "end": v(353.8, 30) * mm});
            skLineSegment(sketch, "E22.7.2.6", {"start": v(355.8, 45) * mm, "end": v(354.8, 45) * mm});
            skLineSegment(sketch, "E22.7.2.7", {"start": v(353.8, 60) * mm, "end": v(352.8, 60) * mm});
            skLineSegment(sketch, "E22.7.2.8", {"start": v(354.8, 15) * mm, "end": v(355.8, 15) * mm});
            skLineSegment(sketch, "E22.7.3.0", {"start": v(355.8, -22.5) * mm, "end": v(355.8, 7.5) * mm});
            skLineSegment(sketch, "E22.7.3.1", {"start": v(352.8, 22.5) * mm, "end": v(352.8, -7.5) * mm});
            skPoint(sketch, "E22.7.3.2", {"position": v(352.8, 7.5) * mm});
            skLineSegment(sketch, "E22.7.3.3", {"start": v(353.8, -7.5) * mm, "end": v(353.8, 22.5) * mm});
            skLineSegment(sketch, "E22.7.3.4", {"start": v(354.8, 7.5) * mm, "end": v(354.8, -22.5) * mm});
            skLineSegment(sketch, "E22.7.3.5", {"start": v(352.8, -7.5) * mm, "end": v(353.8, -7.5) * mm});
            skLineSegment(sketch, "E22.7.3.6", {"start": v(355.8, 7.5) * mm, "end": v(354.8, 7.5) * mm});
            skLineSegment(sketch, "E22.7.3.7", {"start": v(353.8, 22.5) * mm, "end": v(352.8, 22.5) * mm});
            skLineSegment(sketch, "E22.7.3.8", {"start": v(354.8, -22.5) * mm, "end": v(355.8, -22.5) * mm});
            skLineSegment(sketch, "E22.direction1", {"start": v(327.8, 90) * mm, "end": v(331.8, 90) * mm, "construction": true});
            skLineSegment(sketch, "E22.direction2", {"start": v(327.8, 90) * mm, "end": v(327.8, 52.5) * mm, "construction": true});
            skLineSegment(sketch, "E23.0.8.0", {"start": v(359.8, 90) * mm, "end": v(359.8, 120) * mm});
            skLineSegment(sketch, "E23.3.8.0", {"start": v(356.8, 135) * mm, "end": v(356.8, 105) * mm});
            skPoint(sketch, "E23.6.8.0", {"position": v(356.8, 120) * mm});
            skLineSegment(sketch, "E23.7.8.0", {"start": v(357.8, 105) * mm, "end": v(357.8, 135) * mm});
            skLineSegment(sketch, "E23.10.8.0", {"start": v(358.8, 120) * mm, "end": v(358.8, 90) * mm});
            skLineSegment(sketch, "E23.13.8.0", {"start": v(356.8, 105) * mm, "end": v(357.8, 105) * mm});
            skLineSegment(sketch, "E23.16.8.0", {"start": v(359.8, 120) * mm, "end": v(358.8, 120) * mm});
            skLineSegment(sketch, "E23.19.8.0", {"start": v(357.8, 135) * mm, "end": v(356.8, 135) * mm});
            skLineSegment(sketch, "E23.22.8.0", {"start": v(358.8, 90) * mm, "end": v(359.8, 90) * mm});
            skLineSegment(sketch, "E23.0.8.1", {"start": v(359.8, 52.5) * mm, "end": v(359.8, 82.5) * mm});
            skLineSegment(sketch, "E23.3.8.1", {"start": v(356.8, 97.5) * mm, "end": v(356.8, 67.5) * mm});
            skPoint(sketch, "E23.6.8.1", {"position": v(356.8, 82.5) * mm});
            skLineSegment(sketch, "E23.7.8.1", {"start": v(357.8, 67.5) * mm, "end": v(357.8, 97.5) * mm});
            skLineSegment(sketch, "E23.10.8.1", {"start": v(358.8, 82.5) * mm, "end": v(358.8, 52.5) * mm});
            skLineSegment(sketch, "E23.13.8.1", {"start": v(356.8, 67.5) * mm, "end": v(357.8, 67.5) * mm});
            skLineSegment(sketch, "E23.16.8.1", {"start": v(359.8, 82.5) * mm, "end": v(358.8, 82.5) * mm});
            skLineSegment(sketch, "E23.19.8.1", {"start": v(357.8, 97.5) * mm, "end": v(356.8, 97.5) * mm});
            skLineSegment(sketch, "E23.22.8.1", {"start": v(358.8, 52.5) * mm, "end": v(359.8, 52.5) * mm});
            skLineSegment(sketch, "E23.0.8.2", {"start": v(359.8, 15) * mm, "end": v(359.8, 45) * mm});
            skLineSegment(sketch, "E23.3.8.2", {"start": v(356.8, 60) * mm, "end": v(356.8, 30) * mm});
            skPoint(sketch, "E23.6.8.2", {"position": v(356.8, 45) * mm});
            skLineSegment(sketch, "E23.7.8.2", {"start": v(357.8, 30) * mm, "end": v(357.8, 60) * mm});
            skLineSegment(sketch, "E23.10.8.2", {"start": v(358.8, 45) * mm, "end": v(358.8, 15) * mm});
            skLineSegment(sketch, "E23.13.8.2", {"start": v(356.8, 30) * mm, "end": v(357.8, 30) * mm});
            skLineSegment(sketch, "E23.16.8.2", {"start": v(359.8, 45) * mm, "end": v(358.8, 45) * mm});
            skLineSegment(sketch, "E23.19.8.2", {"start": v(357.8, 60) * mm, "end": v(356.8, 60) * mm});
            skLineSegment(sketch, "E23.22.8.2", {"start": v(358.8, 15) * mm, "end": v(359.8, 15) * mm});
            skLineSegment(sketch, "E23.0.8.3", {"start": v(359.8, -22.5) * mm, "end": v(359.8, 7.5) * mm});
            skLineSegment(sketch, "E23.3.8.3", {"start": v(356.8, 22.5) * mm, "end": v(356.8, -7.5) * mm});
            skPoint(sketch, "E23.6.8.3", {"position": v(356.8, 7.5) * mm});
            skLineSegment(sketch, "E23.7.8.3", {"start": v(357.8, -7.5) * mm, "end": v(357.8, 22.5) * mm});
            skLineSegment(sketch, "E23.10.8.3", {"start": v(358.8, 7.5) * mm, "end": v(358.8, -22.5) * mm});
            skLineSegment(sketch, "E23.13.8.3", {"start": v(356.8, -7.5) * mm, "end": v(357.8, -7.5) * mm});
            skLineSegment(sketch, "E23.16.8.3", {"start": v(359.8, 7.5) * mm, "end": v(358.8, 7.5) * mm});
            skLineSegment(sketch, "E23.19.8.3", {"start": v(357.8, 22.5) * mm, "end": v(356.8, 22.5) * mm});
            skLineSegment(sketch, "E23.22.8.3", {"start": v(358.8, -22.5) * mm, "end": v(359.8, -22.5) * mm});
            skLineSegment(sketch, "E23.0.9.0", {"start": v(363.8, 90) * mm, "end": v(363.8, 120) * mm});
            skLineSegment(sketch, "E23.3.9.0", {"start": v(360.8, 135) * mm, "end": v(360.8, 105) * mm});
            skPoint(sketch, "E23.6.9.0", {"position": v(360.8, 120) * mm});
            skLineSegment(sketch, "E23.7.9.0", {"start": v(361.8, 105) * mm, "end": v(361.8, 135) * mm});
            skLineSegment(sketch, "E23.10.9.0", {"start": v(362.8, 120) * mm, "end": v(362.8, 90) * mm});
            skLineSegment(sketch, "E23.13.9.0", {"start": v(360.8, 105) * mm, "end": v(361.8, 105) * mm});
            skLineSegment(sketch, "E23.16.9.0", {"start": v(363.8, 120) * mm, "end": v(362.8, 120) * mm});
            skLineSegment(sketch, "E23.19.9.0", {"start": v(361.8, 135) * mm, "end": v(360.8, 135) * mm});
            skLineSegment(sketch, "E23.22.9.0", {"start": v(362.8, 90) * mm, "end": v(363.8, 90) * mm});
            skLineSegment(sketch, "E23.0.9.1", {"start": v(363.8, 52.5) * mm, "end": v(363.8, 82.5) * mm});
            skLineSegment(sketch, "E23.3.9.1", {"start": v(360.8, 97.5) * mm, "end": v(360.8, 67.5) * mm});
            skPoint(sketch, "E23.6.9.1", {"position": v(360.8, 82.5) * mm});
            skLineSegment(sketch, "E23.7.9.1", {"start": v(361.8, 67.5) * mm, "end": v(361.8, 97.5) * mm});
            skLineSegment(sketch, "E23.10.9.1", {"start": v(362.8, 82.5) * mm, "end": v(362.8, 52.5) * mm});
            skLineSegment(sketch, "E23.13.9.1", {"start": v(360.8, 67.5) * mm, "end": v(361.8, 67.5) * mm});
            skLineSegment(sketch, "E23.16.9.1", {"start": v(363.8, 82.5) * mm, "end": v(362.8, 82.5) * mm});
            skLineSegment(sketch, "E23.19.9.1", {"start": v(361.8, 97.5) * mm, "end": v(360.8, 97.5) * mm});
            skLineSegment(sketch, "E23.22.9.1", {"start": v(362.8, 52.5) * mm, "end": v(363.8, 52.5) * mm});
            skLineSegment(sketch, "E23.0.9.2", {"start": v(363.8, 15) * mm, "end": v(363.8, 45) * mm});
            skLineSegment(sketch, "E23.3.9.2", {"start": v(360.8, 60) * mm, "end": v(360.8, 30) * mm});
            skPoint(sketch, "E23.6.9.2", {"position": v(360.8, 45) * mm});
            skLineSegment(sketch, "E23.7.9.2", {"start": v(361.8, 30) * mm, "end": v(361.8, 60) * mm});
            skLineSegment(sketch, "E23.10.9.2", {"start": v(362.8, 45) * mm, "end": v(362.8, 15) * mm});
            skLineSegment(sketch, "E23.13.9.2", {"start": v(360.8, 30) * mm, "end": v(361.8, 30) * mm});
            skLineSegment(sketch, "E23.16.9.2", {"start": v(363.8, 45) * mm, "end": v(362.8, 45) * mm});
            skLineSegment(sketch, "E23.19.9.2", {"start": v(361.8, 60) * mm, "end": v(360.8, 60) * mm});
            skLineSegment(sketch, "E23.22.9.2", {"start": v(362.8, 15) * mm, "end": v(363.8, 15) * mm});
            skLineSegment(sketch, "E23.0.9.3", {"start": v(363.8, -22.5) * mm, "end": v(363.8, 7.5) * mm});
            skLineSegment(sketch, "E23.3.9.3", {"start": v(360.8, 22.5) * mm, "end": v(360.8, -7.5) * mm});
            skPoint(sketch, "E23.6.9.3", {"position": v(360.8, 7.5) * mm});
            skLineSegment(sketch, "E23.7.9.3", {"start": v(361.8, -7.5) * mm, "end": v(361.8, 22.5) * mm});
            skLineSegment(sketch, "E23.10.9.3", {"start": v(362.8, 7.5) * mm, "end": v(362.8, -22.5) * mm});
            skLineSegment(sketch, "E23.13.9.3", {"start": v(360.8, -7.5) * mm, "end": v(361.8, -7.5) * mm});
            skLineSegment(sketch, "E23.16.9.3", {"start": v(363.8, 7.5) * mm, "end": v(362.8, 7.5) * mm});
            skLineSegment(sketch, "E23.19.9.3", {"start": v(361.8, 22.5) * mm, "end": v(360.8, 22.5) * mm});
            skLineSegment(sketch, "E23.22.9.3", {"start": v(362.8, -22.5) * mm, "end": v(363.8, -22.5) * mm});
            skLineSegment(sketch, "E24.0.10.0", {"start": v(367.8, 90) * mm, "end": v(367.8, 120) * mm});
            skLineSegment(sketch, "E24.3.10.0", {"start": v(364.8, 135) * mm, "end": v(364.8, 105) * mm});
            skPoint(sketch, "E24.6.10.0", {"position": v(364.8, 120) * mm});
            skLineSegment(sketch, "E24.7.10.0", {"start": v(365.8, 105) * mm, "end": v(365.8, 135) * mm});
            skLineSegment(sketch, "E24.10.10.0", {"start": v(366.8, 120) * mm, "end": v(366.8, 90) * mm});
            skLineSegment(sketch, "E24.13.10.0", {"start": v(364.8, 105) * mm, "end": v(365.8, 105) * mm});
            skLineSegment(sketch, "E24.16.10.0", {"start": v(367.8, 120) * mm, "end": v(366.8, 120) * mm});
            skLineSegment(sketch, "E24.19.10.0", {"start": v(365.8, 135) * mm, "end": v(364.8, 135) * mm});
            skLineSegment(sketch, "E24.22.10.0", {"start": v(366.8, 90) * mm, "end": v(367.8, 90) * mm});
            skLineSegment(sketch, "E24.0.10.1", {"start": v(367.8, 52.5) * mm, "end": v(367.8, 82.5) * mm});
            skLineSegment(sketch, "E24.3.10.1", {"start": v(364.8, 97.5) * mm, "end": v(364.8, 67.5) * mm});
            skPoint(sketch, "E24.6.10.1", {"position": v(364.8, 82.5) * mm});
            skLineSegment(sketch, "E24.7.10.1", {"start": v(365.8, 67.5) * mm, "end": v(365.8, 97.5) * mm});
            skLineSegment(sketch, "E24.10.10.1", {"start": v(366.8, 82.5) * mm, "end": v(366.8, 52.5) * mm});
            skLineSegment(sketch, "E24.13.10.1", {"start": v(364.8, 67.5) * mm, "end": v(365.8, 67.5) * mm});
            skLineSegment(sketch, "E24.16.10.1", {"start": v(367.8, 82.5) * mm, "end": v(366.8, 82.5) * mm});
            skLineSegment(sketch, "E24.19.10.1", {"start": v(365.8, 97.5) * mm, "end": v(364.8, 97.5) * mm});
            skLineSegment(sketch, "E24.22.10.1", {"start": v(366.8, 52.5) * mm, "end": v(367.8, 52.5) * mm});
            skLineSegment(sketch, "E24.0.10.2", {"start": v(367.8, 15) * mm, "end": v(367.8, 45) * mm});
            skLineSegment(sketch, "E24.3.10.2", {"start": v(364.8, 60) * mm, "end": v(364.8, 30) * mm});
            skPoint(sketch, "E24.6.10.2", {"position": v(364.8, 45) * mm});
            skLineSegment(sketch, "E24.7.10.2", {"start": v(365.8, 30) * mm, "end": v(365.8, 60) * mm});
            skLineSegment(sketch, "E24.10.10.2", {"start": v(366.8, 45) * mm, "end": v(366.8, 15) * mm});
            skLineSegment(sketch, "E24.13.10.2", {"start": v(364.8, 30) * mm, "end": v(365.8, 30) * mm});
            skLineSegment(sketch, "E24.16.10.2", {"start": v(367.8, 45) * mm, "end": v(366.8, 45) * mm});
            skLineSegment(sketch, "E24.19.10.2", {"start": v(365.8, 60) * mm, "end": v(364.8, 60) * mm});
            skLineSegment(sketch, "E24.22.10.2", {"start": v(366.8, 15) * mm, "end": v(367.8, 15) * mm});
            skLineSegment(sketch, "E24.0.10.3", {"start": v(367.8, -22.5) * mm, "end": v(367.8, 7.5) * mm});
            skLineSegment(sketch, "E24.3.10.3", {"start": v(364.8, 22.5) * mm, "end": v(364.8, -7.5) * mm});
            skPoint(sketch, "E24.6.10.3", {"position": v(364.8, 7.5) * mm});
            skLineSegment(sketch, "E24.7.10.3", {"start": v(365.8, -7.5) * mm, "end": v(365.8, 22.5) * mm});
            skLineSegment(sketch, "E24.10.10.3", {"start": v(366.8, 7.5) * mm, "end": v(366.8, -22.5) * mm});
            skLineSegment(sketch, "E24.13.10.3", {"start": v(364.8, -7.5) * mm, "end": v(365.8, -7.5) * mm});
            skLineSegment(sketch, "E24.16.10.3", {"start": v(367.8, 7.5) * mm, "end": v(366.8, 7.5) * mm});
            skLineSegment(sketch, "E24.19.10.3", {"start": v(365.8, 22.5) * mm, "end": v(364.8, 22.5) * mm});
            skLineSegment(sketch, "E24.22.10.3", {"start": v(366.8, -22.5) * mm, "end": v(367.8, -22.5) * mm});
            skLineSegment(sketch, "E25.0.11.0", {"start": v(371.8, 90) * mm, "end": v(371.8, 120) * mm});
            skLineSegment(sketch, "E25.3.11.0", {"start": v(368.8, 135) * mm, "end": v(368.8, 105) * mm});
            skPoint(sketch, "E25.6.11.0", {"position": v(368.8, 120) * mm});
            skLineSegment(sketch, "E25.7.11.0", {"start": v(369.8, 105) * mm, "end": v(369.8, 135) * mm});
            skLineSegment(sketch, "E25.10.11.0", {"start": v(370.8, 120) * mm, "end": v(370.8, 90) * mm});
            skLineSegment(sketch, "E25.13.11.0", {"start": v(368.8, 105) * mm, "end": v(369.8, 105) * mm});
            skLineSegment(sketch, "E25.16.11.0", {"start": v(371.8, 120) * mm, "end": v(370.8, 120) * mm});
            skLineSegment(sketch, "E25.19.11.0", {"start": v(369.8, 135) * mm, "end": v(368.8, 135) * mm});
            skLineSegment(sketch, "E25.22.11.0", {"start": v(370.8, 90) * mm, "end": v(371.8, 90) * mm});
            skLineSegment(sketch, "E25.0.11.1", {"start": v(371.8, 52.5) * mm, "end": v(371.8, 82.5) * mm});
            skLineSegment(sketch, "E25.3.11.1", {"start": v(368.8, 97.5) * mm, "end": v(368.8, 67.5) * mm});
            skPoint(sketch, "E25.6.11.1", {"position": v(368.8, 82.5) * mm});
            skLineSegment(sketch, "E25.7.11.1", {"start": v(369.8, 67.5) * mm, "end": v(369.8, 97.5) * mm});
            skLineSegment(sketch, "E25.10.11.1", {"start": v(370.8, 82.5) * mm, "end": v(370.8, 52.5) * mm});
            skLineSegment(sketch, "E25.13.11.1", {"start": v(368.8, 67.5) * mm, "end": v(369.8, 67.5) * mm});
            skLineSegment(sketch, "E25.16.11.1", {"start": v(371.8, 82.5) * mm, "end": v(370.8, 82.5) * mm});
            skLineSegment(sketch, "E25.19.11.1", {"start": v(369.8, 97.5) * mm, "end": v(368.8, 97.5) * mm});
            skLineSegment(sketch, "E25.22.11.1", {"start": v(370.8, 52.5) * mm, "end": v(371.8, 52.5) * mm});
            skLineSegment(sketch, "E25.0.11.2", {"start": v(371.8, 15) * mm, "end": v(371.8, 45) * mm});
            skLineSegment(sketch, "E25.3.11.2", {"start": v(368.8, 60) * mm, "end": v(368.8, 30) * mm});
            skPoint(sketch, "E25.6.11.2", {"position": v(368.8, 45) * mm});
            skLineSegment(sketch, "E25.7.11.2", {"start": v(369.8, 30) * mm, "end": v(369.8, 60) * mm});
            skLineSegment(sketch, "E25.10.11.2", {"start": v(370.8, 45) * mm, "end": v(370.8, 15) * mm});
            skLineSegment(sketch, "E25.13.11.2", {"start": v(368.8, 30) * mm, "end": v(369.8, 30) * mm});
            skLineSegment(sketch, "E25.16.11.2", {"start": v(371.8, 45) * mm, "end": v(370.8, 45) * mm});
            skLineSegment(sketch, "E25.19.11.2", {"start": v(369.8, 60) * mm, "end": v(368.8, 60) * mm});
            skLineSegment(sketch, "E25.22.11.2", {"start": v(370.8, 15) * mm, "end": v(371.8, 15) * mm});
            skLineSegment(sketch, "E25.0.11.3", {"start": v(371.8, -22.5) * mm, "end": v(371.8, 7.5) * mm});
            skLineSegment(sketch, "E25.3.11.3", {"start": v(368.8, 22.5) * mm, "end": v(368.8, -7.5) * mm});
            skPoint(sketch, "E25.6.11.3", {"position": v(368.8, 7.5) * mm});
            skLineSegment(sketch, "E25.7.11.3", {"start": v(369.8, -7.5) * mm, "end": v(369.8, 22.5) * mm});
            skLineSegment(sketch, "E25.10.11.3", {"start": v(370.8, 7.5) * mm, "end": v(370.8, -22.5) * mm});
            skLineSegment(sketch, "E25.13.11.3", {"start": v(368.8, -7.5) * mm, "end": v(369.8, -7.5) * mm});
            skLineSegment(sketch, "E25.16.11.3", {"start": v(371.8, 7.5) * mm, "end": v(370.8, 7.5) * mm});
            skLineSegment(sketch, "E25.19.11.3", {"start": v(369.8, 22.5) * mm, "end": v(368.8, 22.5) * mm});
            skLineSegment(sketch, "E25.22.11.3", {"start": v(370.8, -22.5) * mm, "end": v(371.8, -22.5) * mm});
            skLineSegment(sketch, "E26.0.12.0", {"start": v(375.8, 90) * mm, "end": v(375.8, 120) * mm});
            skLineSegment(sketch, "E26.3.12.0", {"start": v(372.8, 135) * mm, "end": v(372.8, 105) * mm});
            skPoint(sketch, "E26.6.12.0", {"position": v(372.8, 120) * mm});
            skLineSegment(sketch, "E26.7.12.0", {"start": v(373.8, 105) * mm, "end": v(373.8, 135) * mm});
            skLineSegment(sketch, "E26.10.12.0", {"start": v(374.8, 120) * mm, "end": v(374.8, 90) * mm});
            skLineSegment(sketch, "E26.13.12.0", {"start": v(372.8, 105) * mm, "end": v(373.8, 105) * mm});
            skLineSegment(sketch, "E26.16.12.0", {"start": v(375.8, 120) * mm, "end": v(374.8, 120) * mm});
            skLineSegment(sketch, "E26.19.12.0", {"start": v(373.8, 135) * mm, "end": v(372.8, 135) * mm});
            skLineSegment(sketch, "E26.22.12.0", {"start": v(374.8, 90) * mm, "end": v(375.8, 90) * mm});
            skLineSegment(sketch, "E26.0.12.1", {"start": v(375.8, 52.5) * mm, "end": v(375.8, 82.5) * mm});
            skLineSegment(sketch, "E26.3.12.1", {"start": v(372.8, 97.5) * mm, "end": v(372.8, 67.5) * mm});
            skPoint(sketch, "E26.6.12.1", {"position": v(372.8, 82.5) * mm});
            skLineSegment(sketch, "E26.7.12.1", {"start": v(373.8, 67.5) * mm, "end": v(373.8, 97.5) * mm});
            skLineSegment(sketch, "E26.10.12.1", {"start": v(374.8, 82.5) * mm, "end": v(374.8, 52.5) * mm});
            skLineSegment(sketch, "E26.13.12.1", {"start": v(372.8, 67.5) * mm, "end": v(373.8, 67.5) * mm});
            skLineSegment(sketch, "E26.16.12.1", {"start": v(375.8, 82.5) * mm, "end": v(374.8, 82.5) * mm});
            skLineSegment(sketch, "E26.19.12.1", {"start": v(373.8, 97.5) * mm, "end": v(372.8, 97.5) * mm});
            skLineSegment(sketch, "E26.22.12.1", {"start": v(374.8, 52.5) * mm, "end": v(375.8, 52.5) * mm});
            skLineSegment(sketch, "E26.0.12.2", {"start": v(375.8, 15) * mm, "end": v(375.8, 45) * mm});
            skLineSegment(sketch, "E26.3.12.2", {"start": v(372.8, 60) * mm, "end": v(372.8, 30) * mm});
            skPoint(sketch, "E26.6.12.2", {"position": v(372.8, 45) * mm});
            skLineSegment(sketch, "E26.7.12.2", {"start": v(373.8, 30) * mm, "end": v(373.8, 60) * mm});
            skLineSegment(sketch, "E26.10.12.2", {"start": v(374.8, 45) * mm, "end": v(374.8, 15) * mm});
            skLineSegment(sketch, "E26.13.12.2", {"start": v(372.8, 30) * mm, "end": v(373.8, 30) * mm});
            skLineSegment(sketch, "E26.16.12.2", {"start": v(375.8, 45) * mm, "end": v(374.8, 45) * mm});
            skLineSegment(sketch, "E26.19.12.2", {"start": v(373.8, 60) * mm, "end": v(372.8, 60) * mm});
            skLineSegment(sketch, "E26.22.12.2", {"start": v(374.8, 15) * mm, "end": v(375.8, 15) * mm});
            skLineSegment(sketch, "E26.0.12.3", {"start": v(375.8, -22.5) * mm, "end": v(375.8, 7.5) * mm});
            skLineSegment(sketch, "E26.3.12.3", {"start": v(372.8, 22.5) * mm, "end": v(372.8, -7.5) * mm});
            skPoint(sketch, "E26.6.12.3", {"position": v(372.8, 7.5) * mm});
            skLineSegment(sketch, "E26.7.12.3", {"start": v(373.8, -7.5) * mm, "end": v(373.8, 22.5) * mm});
            skLineSegment(sketch, "E26.10.12.3", {"start": v(374.8, 7.5) * mm, "end": v(374.8, -22.5) * mm});
            skLineSegment(sketch, "E26.13.12.3", {"start": v(372.8, -7.5) * mm, "end": v(373.8, -7.5) * mm});
            skLineSegment(sketch, "E26.16.12.3", {"start": v(375.8, 7.5) * mm, "end": v(374.8, 7.5) * mm});
            skLineSegment(sketch, "E26.19.12.3", {"start": v(373.8, 22.5) * mm, "end": v(372.8, 22.5) * mm});
            skLineSegment(sketch, "E26.22.12.3", {"start": v(374.8, -22.5) * mm, "end": v(375.8, -22.5) * mm});
            skLineSegment(sketch, "E27.0.13.0", {"start": v(379.8, 90) * mm, "end": v(379.8, 120) * mm});
            skLineSegment(sketch, "E27.3.13.0", {"start": v(376.8, 135) * mm, "end": v(376.8, 105) * mm});
            skPoint(sketch, "E27.6.13.0", {"position": v(376.8, 120) * mm});
            skLineSegment(sketch, "E27.7.13.0", {"start": v(377.8, 105) * mm, "end": v(377.8, 135) * mm});
            skLineSegment(sketch, "E27.10.13.0", {"start": v(378.8, 120) * mm, "end": v(378.8, 90) * mm});
            skLineSegment(sketch, "E27.13.13.0", {"start": v(376.8, 105) * mm, "end": v(377.8, 105) * mm});
            skLineSegment(sketch, "E27.16.13.0", {"start": v(379.8, 120) * mm, "end": v(378.8, 120) * mm});
            skLineSegment(sketch, "E27.19.13.0", {"start": v(377.8, 135) * mm, "end": v(376.8, 135) * mm});
            skLineSegment(sketch, "E27.22.13.0", {"start": v(378.8, 90) * mm, "end": v(379.8, 90) * mm});
            skLineSegment(sketch, "E27.0.13.1", {"start": v(379.8, 52.5) * mm, "end": v(379.8, 82.5) * mm});
            skLineSegment(sketch, "E27.3.13.1", {"start": v(376.8, 97.5) * mm, "end": v(376.8, 67.5) * mm});
            skPoint(sketch, "E27.6.13.1", {"position": v(376.8, 82.5) * mm});
            skLineSegment(sketch, "E27.7.13.1", {"start": v(377.8, 67.5) * mm, "end": v(377.8, 97.5) * mm});
            skLineSegment(sketch, "E27.10.13.1", {"start": v(378.8, 82.5) * mm, "end": v(378.8, 52.5) * mm});
            skLineSegment(sketch, "E27.13.13.1", {"start": v(376.8, 67.5) * mm, "end": v(377.8, 67.5) * mm});
            skLineSegment(sketch, "E27.16.13.1", {"start": v(379.8, 82.5) * mm, "end": v(378.8, 82.5) * mm});
            skLineSegment(sketch, "E27.19.13.1", {"start": v(377.8, 97.5) * mm, "end": v(376.8, 97.5) * mm});
            skLineSegment(sketch, "E27.22.13.1", {"start": v(378.8, 52.5) * mm, "end": v(379.8, 52.5) * mm});
            skLineSegment(sketch, "E27.0.13.2", {"start": v(379.8, 15) * mm, "end": v(379.8, 45) * mm});
            skLineSegment(sketch, "E27.3.13.2", {"start": v(376.8, 60) * mm, "end": v(376.8, 30) * mm});
            skPoint(sketch, "E27.6.13.2", {"position": v(376.8, 45) * mm});
            skLineSegment(sketch, "E27.7.13.2", {"start": v(377.8, 30) * mm, "end": v(377.8, 60) * mm});
            skLineSegment(sketch, "E27.10.13.2", {"start": v(378.8, 45) * mm, "end": v(378.8, 15) * mm});
            skLineSegment(sketch, "E27.13.13.2", {"start": v(376.8, 30) * mm, "end": v(377.8, 30) * mm});
            skLineSegment(sketch, "E27.16.13.2", {"start": v(379.8, 45) * mm, "end": v(378.8, 45) * mm});
            skLineSegment(sketch, "E27.19.13.2", {"start": v(377.8, 60) * mm, "end": v(376.8, 60) * mm});
            skLineSegment(sketch, "E27.22.13.2", {"start": v(378.8, 15) * mm, "end": v(379.8, 15) * mm});
            skLineSegment(sketch, "E27.0.13.3", {"start": v(379.8, -22.5) * mm, "end": v(379.8, 7.5) * mm});
            skLineSegment(sketch, "E27.3.13.3", {"start": v(376.8, 22.5) * mm, "end": v(376.8, -7.5) * mm});
            skPoint(sketch, "E27.6.13.3", {"position": v(376.8, 7.5) * mm});
            skLineSegment(sketch, "E27.7.13.3", {"start": v(377.8, -7.5) * mm, "end": v(377.8, 22.5) * mm});
            skLineSegment(sketch, "E27.10.13.3", {"start": v(378.8, 7.5) * mm, "end": v(378.8, -22.5) * mm});
            skLineSegment(sketch, "E27.13.13.3", {"start": v(376.8, -7.5) * mm, "end": v(377.8, -7.5) * mm});
            skLineSegment(sketch, "E27.16.13.3", {"start": v(379.8, 7.5) * mm, "end": v(378.8, 7.5) * mm});
            skLineSegment(sketch, "E27.19.13.3", {"start": v(377.8, 22.5) * mm, "end": v(376.8, 22.5) * mm});
            skLineSegment(sketch, "E27.22.13.3", {"start": v(378.8, -22.5) * mm, "end": v(379.8, -22.5) * mm});
            skLineSegment(sketch, "E27.0.14.0", {"start": v(383.8, 90) * mm, "end": v(383.8, 120) * mm});
            skLineSegment(sketch, "E27.3.14.0", {"start": v(380.8, 135) * mm, "end": v(380.8, 105) * mm});
            skPoint(sketch, "E27.6.14.0", {"position": v(380.8, 120) * mm});
            skLineSegment(sketch, "E27.7.14.0", {"start": v(381.8, 105) * mm, "end": v(381.8, 135) * mm});
            skLineSegment(sketch, "E27.10.14.0", {"start": v(382.8, 120) * mm, "end": v(382.8, 90) * mm});
            skLineSegment(sketch, "E27.13.14.0", {"start": v(380.8, 105) * mm, "end": v(381.8, 105) * mm});
            skLineSegment(sketch, "E27.16.14.0", {"start": v(383.8, 120) * mm, "end": v(382.8, 120) * mm});
            skLineSegment(sketch, "E27.19.14.0", {"start": v(381.8, 135) * mm, "end": v(380.8, 135) * mm});
            skLineSegment(sketch, "E27.22.14.0", {"start": v(382.8, 90) * mm, "end": v(383.8, 90) * mm});
            skLineSegment(sketch, "E27.0.14.1", {"start": v(383.8, 52.5) * mm, "end": v(383.8, 82.5) * mm});
            skLineSegment(sketch, "E27.3.14.1", {"start": v(380.8, 97.5) * mm, "end": v(380.8, 67.5) * mm});
            skPoint(sketch, "E27.6.14.1", {"position": v(380.8, 82.5) * mm});
            skLineSegment(sketch, "E27.7.14.1", {"start": v(381.8, 67.5) * mm, "end": v(381.8, 97.5) * mm});
            skLineSegment(sketch, "E27.10.14.1", {"start": v(382.8, 82.5) * mm, "end": v(382.8, 52.5) * mm});
            skLineSegment(sketch, "E27.13.14.1", {"start": v(380.8, 67.5) * mm, "end": v(381.8, 67.5) * mm});
            skLineSegment(sketch, "E27.16.14.1", {"start": v(383.8, 82.5) * mm, "end": v(382.8, 82.5) * mm});
            skLineSegment(sketch, "E27.19.14.1", {"start": v(381.8, 97.5) * mm, "end": v(380.8, 97.5) * mm});
            skLineSegment(sketch, "E27.22.14.1", {"start": v(382.8, 52.5) * mm, "end": v(383.8, 52.5) * mm});
            skLineSegment(sketch, "E27.0.14.2", {"start": v(383.8, 15) * mm, "end": v(383.8, 45) * mm});
            skLineSegment(sketch, "E27.3.14.2", {"start": v(380.8, 60) * mm, "end": v(380.8, 30) * mm});
            skPoint(sketch, "E27.6.14.2", {"position": v(380.8, 45) * mm});
            skLineSegment(sketch, "E27.7.14.2", {"start": v(381.8, 30) * mm, "end": v(381.8, 60) * mm});
            skLineSegment(sketch, "E27.10.14.2", {"start": v(382.8, 45) * mm, "end": v(382.8, 15) * mm});
            skLineSegment(sketch, "E27.13.14.2", {"start": v(380.8, 30) * mm, "end": v(381.8, 30) * mm});
            skLineSegment(sketch, "E27.16.14.2", {"start": v(383.8, 45) * mm, "end": v(382.8, 45) * mm});
            skLineSegment(sketch, "E27.19.14.2", {"start": v(381.8, 60) * mm, "end": v(380.8, 60) * mm});
            skLineSegment(sketch, "E27.22.14.2", {"start": v(382.8, 15) * mm, "end": v(383.8, 15) * mm});
            skLineSegment(sketch, "E27.0.14.3", {"start": v(383.8, -22.5) * mm, "end": v(383.8, 7.5) * mm});
            skLineSegment(sketch, "E27.3.14.3", {"start": v(380.8, 22.5) * mm, "end": v(380.8, -7.5) * mm});
            skPoint(sketch, "E27.6.14.3", {"position": v(380.8, 7.5) * mm});
            skLineSegment(sketch, "E27.7.14.3", {"start": v(381.8, -7.5) * mm, "end": v(381.8, 22.5) * mm});
            skLineSegment(sketch, "E27.10.14.3", {"start": v(382.8, 7.5) * mm, "end": v(382.8, -22.5) * mm});
            skLineSegment(sketch, "E27.13.14.3", {"start": v(380.8, -7.5) * mm, "end": v(381.8, -7.5) * mm});
            skLineSegment(sketch, "E27.16.14.3", {"start": v(383.8, 7.5) * mm, "end": v(382.8, 7.5) * mm});
            skLineSegment(sketch, "E27.19.14.3", {"start": v(381.8, 22.5) * mm, "end": v(380.8, 22.5) * mm});
            skLineSegment(sketch, "E27.22.14.3", {"start": v(382.8, -22.5) * mm, "end": v(383.8, -22.5) * mm});
            skLineSegment(sketch, "E27.0.15.0", {"start": v(387.8, 90) * mm, "end": v(387.8, 120) * mm});
            skLineSegment(sketch, "E27.3.15.0", {"start": v(384.8, 135) * mm, "end": v(384.8, 105) * mm});
            skPoint(sketch, "E27.6.15.0", {"position": v(384.8, 120) * mm});
            skLineSegment(sketch, "E27.7.15.0", {"start": v(385.8, 105) * mm, "end": v(385.8, 135) * mm});
            skLineSegment(sketch, "E27.10.15.0", {"start": v(386.8, 120) * mm, "end": v(386.8, 90) * mm});
            skLineSegment(sketch, "E27.13.15.0", {"start": v(384.8, 105) * mm, "end": v(385.8, 105) * mm});
            skLineSegment(sketch, "E27.16.15.0", {"start": v(387.8, 120) * mm, "end": v(386.8, 120) * mm});
            skLineSegment(sketch, "E27.19.15.0", {"start": v(385.8, 135) * mm, "end": v(384.8, 135) * mm});
            skLineSegment(sketch, "E27.22.15.0", {"start": v(386.8, 90) * mm, "end": v(387.8, 90) * mm});
            skLineSegment(sketch, "E27.0.15.1", {"start": v(387.8, 52.5) * mm, "end": v(387.8, 82.5) * mm});
            skLineSegment(sketch, "E27.3.15.1", {"start": v(384.8, 97.5) * mm, "end": v(384.8, 67.5) * mm});
            skPoint(sketch, "E27.6.15.1", {"position": v(384.8, 82.5) * mm});
            skLineSegment(sketch, "E27.7.15.1", {"start": v(385.8, 67.5) * mm, "end": v(385.8, 97.5) * mm});
            skLineSegment(sketch, "E27.10.15.1", {"start": v(386.8, 82.5) * mm, "end": v(386.8, 52.5) * mm});
            skLineSegment(sketch, "E27.13.15.1", {"start": v(384.8, 67.5) * mm, "end": v(385.8, 67.5) * mm});
            skLineSegment(sketch, "E27.16.15.1", {"start": v(387.8, 82.5) * mm, "end": v(386.8, 82.5) * mm});
            skLineSegment(sketch, "E27.19.15.1", {"start": v(385.8, 97.5) * mm, "end": v(384.8, 97.5) * mm});
            skLineSegment(sketch, "E27.22.15.1", {"start": v(386.8, 52.5) * mm, "end": v(387.8, 52.5) * mm});
            skLineSegment(sketch, "E27.0.15.2", {"start": v(387.8, 15) * mm, "end": v(387.8, 45) * mm});
            skLineSegment(sketch, "E27.3.15.2", {"start": v(384.8, 60) * mm, "end": v(384.8, 30) * mm});
            skPoint(sketch, "E27.6.15.2", {"position": v(384.8, 45) * mm});
            skLineSegment(sketch, "E27.7.15.2", {"start": v(385.8, 30) * mm, "end": v(385.8, 60) * mm});
            skLineSegment(sketch, "E27.10.15.2", {"start": v(386.8, 45) * mm, "end": v(386.8, 15) * mm});
            skLineSegment(sketch, "E27.13.15.2", {"start": v(384.8, 30) * mm, "end": v(385.8, 30) * mm});
            skLineSegment(sketch, "E27.16.15.2", {"start": v(387.8, 45) * mm, "end": v(386.8, 45) * mm});
            skLineSegment(sketch, "E27.19.15.2", {"start": v(385.8, 60) * mm, "end": v(384.8, 60) * mm});
            skLineSegment(sketch, "E27.22.15.2", {"start": v(386.8, 15) * mm, "end": v(387.8, 15) * mm});
            skLineSegment(sketch, "E27.0.15.3", {"start": v(387.8, -22.5) * mm, "end": v(387.8, 7.5) * mm});
            skLineSegment(sketch, "E27.3.15.3", {"start": v(384.8, 22.5) * mm, "end": v(384.8, -7.5) * mm});
            skPoint(sketch, "E27.6.15.3", {"position": v(384.8, 7.5) * mm});
            skLineSegment(sketch, "E27.7.15.3", {"start": v(385.8, -7.5) * mm, "end": v(385.8, 22.5) * mm});
            skLineSegment(sketch, "E27.10.15.3", {"start": v(386.8, 7.5) * mm, "end": v(386.8, -22.5) * mm});
            skLineSegment(sketch, "E27.13.15.3", {"start": v(384.8, -7.5) * mm, "end": v(385.8, -7.5) * mm});
            skLineSegment(sketch, "E27.16.15.3", {"start": v(387.8, 7.5) * mm, "end": v(386.8, 7.5) * mm});
            skLineSegment(sketch, "E27.19.15.3", {"start": v(385.8, 22.5) * mm, "end": v(384.8, 22.5) * mm});
            skLineSegment(sketch, "E27.22.15.3", {"start": v(386.8, -22.5) * mm, "end": v(387.8, -22.5) * mm});
            skLineSegment(sketch, "E27.0.16.0", {"start": v(391.8, 90) * mm, "end": v(391.8, 120) * mm});
            skLineSegment(sketch, "E27.3.16.0", {"start": v(388.8, 135) * mm, "end": v(388.8, 105) * mm});
            skPoint(sketch, "E27.6.16.0", {"position": v(388.8, 120) * mm});
            skLineSegment(sketch, "E27.7.16.0", {"start": v(389.8, 105) * mm, "end": v(389.8, 135) * mm});
            skLineSegment(sketch, "E27.10.16.0", {"start": v(390.8, 120) * mm, "end": v(390.8, 90) * mm});
            skLineSegment(sketch, "E27.13.16.0", {"start": v(388.8, 105) * mm, "end": v(389.8, 105) * mm});
            skLineSegment(sketch, "E27.16.16.0", {"start": v(391.8, 120) * mm, "end": v(390.8, 120) * mm});
            skLineSegment(sketch, "E27.19.16.0", {"start": v(389.8, 135) * mm, "end": v(388.8, 135) * mm});
            skLineSegment(sketch, "E27.22.16.0", {"start": v(390.8, 90) * mm, "end": v(391.8, 90) * mm});
            skLineSegment(sketch, "E27.0.16.1", {"start": v(391.8, 52.5) * mm, "end": v(391.8, 82.5) * mm});
            skLineSegment(sketch, "E27.3.16.1", {"start": v(388.8, 97.5) * mm, "end": v(388.8, 67.5) * mm});
            skPoint(sketch, "E27.6.16.1", {"position": v(388.8, 82.5) * mm});
            skLineSegment(sketch, "E27.7.16.1", {"start": v(389.8, 67.5) * mm, "end": v(389.8, 97.5) * mm});
            skLineSegment(sketch, "E27.10.16.1", {"start": v(390.8, 82.5) * mm, "end": v(390.8, 52.5) * mm});
            skLineSegment(sketch, "E27.13.16.1", {"start": v(388.8, 67.5) * mm, "end": v(389.8, 67.5) * mm});
            skLineSegment(sketch, "E27.16.16.1", {"start": v(391.8, 82.5) * mm, "end": v(390.8, 82.5) * mm});
            skLineSegment(sketch, "E27.19.16.1", {"start": v(389.8, 97.5) * mm, "end": v(388.8, 97.5) * mm});
            skLineSegment(sketch, "E27.22.16.1", {"start": v(390.8, 52.5) * mm, "end": v(391.8, 52.5) * mm});
            skLineSegment(sketch, "E27.0.16.2", {"start": v(391.8, 15) * mm, "end": v(391.8, 45) * mm});
            skLineSegment(sketch, "E27.3.16.2", {"start": v(388.8, 60) * mm, "end": v(388.8, 30) * mm});
            skPoint(sketch, "E27.6.16.2", {"position": v(388.8, 45) * mm});
            skLineSegment(sketch, "E27.7.16.2", {"start": v(389.8, 30) * mm, "end": v(389.8, 60) * mm});
            skLineSegment(sketch, "E27.10.16.2", {"start": v(390.8, 45) * mm, "end": v(390.8, 15) * mm});
            skLineSegment(sketch, "E27.13.16.2", {"start": v(388.8, 30) * mm, "end": v(389.8, 30) * mm});
            skLineSegment(sketch, "E27.16.16.2", {"start": v(391.8, 45) * mm, "end": v(390.8, 45) * mm});
            skLineSegment(sketch, "E27.19.16.2", {"start": v(389.8, 60) * mm, "end": v(388.8, 60) * mm});
            skLineSegment(sketch, "E27.22.16.2", {"start": v(390.8, 15) * mm, "end": v(391.8, 15) * mm});
            skLineSegment(sketch, "E27.0.16.3", {"start": v(391.8, -22.5) * mm, "end": v(391.8, 7.5) * mm});
            skLineSegment(sketch, "E27.3.16.3", {"start": v(388.8, 22.5) * mm, "end": v(388.8, -7.5) * mm});
            skPoint(sketch, "E27.6.16.3", {"position": v(388.8, 7.5) * mm});
            skLineSegment(sketch, "E27.7.16.3", {"start": v(389.8, -7.5) * mm, "end": v(389.8, 22.5) * mm});
            skLineSegment(sketch, "E27.10.16.3", {"start": v(390.8, 7.5) * mm, "end": v(390.8, -22.5) * mm});
            skLineSegment(sketch, "E27.13.16.3", {"start": v(388.8, -7.5) * mm, "end": v(389.8, -7.5) * mm});
            skLineSegment(sketch, "E27.16.16.3", {"start": v(391.8, 7.5) * mm, "end": v(390.8, 7.5) * mm});
            skLineSegment(sketch, "E27.19.16.3", {"start": v(389.8, 22.5) * mm, "end": v(388.8, 22.5) * mm});
            skLineSegment(sketch, "E27.22.16.3", {"start": v(390.8, -22.5) * mm, "end": v(391.8, -22.5) * mm});
            skLineSegment(sketch, "E27.0.17.0", {"start": v(395.8, 90) * mm, "end": v(395.8, 120) * mm});
            skLineSegment(sketch, "E27.3.17.0", {"start": v(392.8, 135) * mm, "end": v(392.8, 105) * mm});
            skPoint(sketch, "E27.6.17.0", {"position": v(392.8, 120) * mm});
            skLineSegment(sketch, "E27.7.17.0", {"start": v(393.8, 105) * mm, "end": v(393.8, 135) * mm});
            skLineSegment(sketch, "E27.10.17.0", {"start": v(394.8, 120) * mm, "end": v(394.8, 90) * mm});
            skLineSegment(sketch, "E27.13.17.0", {"start": v(392.8, 105) * mm, "end": v(393.8, 105) * mm});
            skLineSegment(sketch, "E27.16.17.0", {"start": v(395.8, 120) * mm, "end": v(394.8, 120) * mm});
            skLineSegment(sketch, "E27.19.17.0", {"start": v(393.8, 135) * mm, "end": v(392.8, 135) * mm});
            skLineSegment(sketch, "E27.22.17.0", {"start": v(394.8, 90) * mm, "end": v(395.8, 90) * mm});
            skLineSegment(sketch, "E27.0.17.1", {"start": v(395.8, 52.5) * mm, "end": v(395.8, 82.5) * mm});
            skLineSegment(sketch, "E27.3.17.1", {"start": v(392.8, 97.5) * mm, "end": v(392.8, 67.5) * mm});
            skPoint(sketch, "E27.6.17.1", {"position": v(392.8, 82.5) * mm});
            skLineSegment(sketch, "E27.7.17.1", {"start": v(393.8, 67.5) * mm, "end": v(393.8, 97.5) * mm});
            skLineSegment(sketch, "E27.10.17.1", {"start": v(394.8, 82.5) * mm, "end": v(394.8, 52.5) * mm});
            skLineSegment(sketch, "E27.13.17.1", {"start": v(392.8, 67.5) * mm, "end": v(393.8, 67.5) * mm});
            skLineSegment(sketch, "E27.16.17.1", {"start": v(395.8, 82.5) * mm, "end": v(394.8, 82.5) * mm});
            skLineSegment(sketch, "E27.19.17.1", {"start": v(393.8, 97.5) * mm, "end": v(392.8, 97.5) * mm});
            skLineSegment(sketch, "E27.22.17.1", {"start": v(394.8, 52.5) * mm, "end": v(395.8, 52.5) * mm});
            skLineSegment(sketch, "E27.0.17.2", {"start": v(395.8, 15) * mm, "end": v(395.8, 45) * mm});
            skLineSegment(sketch, "E27.3.17.2", {"start": v(392.8, 60) * mm, "end": v(392.8, 30) * mm});
            skPoint(sketch, "E27.6.17.2", {"position": v(392.8, 45) * mm});
            skLineSegment(sketch, "E27.7.17.2", {"start": v(393.8, 30) * mm, "end": v(393.8, 60) * mm});
            skLineSegment(sketch, "E27.10.17.2", {"start": v(394.8, 45) * mm, "end": v(394.8, 15) * mm});
            skLineSegment(sketch, "E27.13.17.2", {"start": v(392.8, 30) * mm, "end": v(393.8, 30) * mm});
            skLineSegment(sketch, "E27.16.17.2", {"start": v(395.8, 45) * mm, "end": v(394.8, 45) * mm});
            skLineSegment(sketch, "E27.19.17.2", {"start": v(393.8, 60) * mm, "end": v(392.8, 60) * mm});
            skLineSegment(sketch, "E27.22.17.2", {"start": v(394.8, 15) * mm, "end": v(395.8, 15) * mm});
            skLineSegment(sketch, "E27.0.17.3", {"start": v(395.8, -22.5) * mm, "end": v(395.8, 7.5) * mm});
            skLineSegment(sketch, "E27.3.17.3", {"start": v(392.8, 22.5) * mm, "end": v(392.8, -7.5) * mm});
            skPoint(sketch, "E27.6.17.3", {"position": v(392.8, 7.5) * mm});
            skLineSegment(sketch, "E27.7.17.3", {"start": v(393.8, -7.5) * mm, "end": v(393.8, 22.5) * mm});
            skLineSegment(sketch, "E27.10.17.3", {"start": v(394.8, 7.5) * mm, "end": v(394.8, -22.5) * mm});
            skLineSegment(sketch, "E27.13.17.3", {"start": v(392.8, -7.5) * mm, "end": v(393.8, -7.5) * mm});
            skLineSegment(sketch, "E27.16.17.3", {"start": v(395.8, 7.5) * mm, "end": v(394.8, 7.5) * mm});
            skLineSegment(sketch, "E27.19.17.3", {"start": v(393.8, 22.5) * mm, "end": v(392.8, 22.5) * mm});
            skLineSegment(sketch, "E27.22.17.3", {"start": v(394.8, -22.5) * mm, "end": v(395.8, -22.5) * mm});
            skLineSegment(sketch, "E27.0.18.0", {"start": v(399.8, 90) * mm, "end": v(399.8, 120) * mm});
            skLineSegment(sketch, "E27.3.18.0", {"start": v(396.8, 135) * mm, "end": v(396.8, 105) * mm});
            skPoint(sketch, "E27.6.18.0", {"position": v(396.8, 120) * mm});
            skLineSegment(sketch, "E27.7.18.0", {"start": v(397.8, 105) * mm, "end": v(397.8, 135) * mm});
            skLineSegment(sketch, "E27.10.18.0", {"start": v(398.8, 120) * mm, "end": v(398.8, 90) * mm});
            skLineSegment(sketch, "E27.13.18.0", {"start": v(396.8, 105) * mm, "end": v(397.8, 105) * mm});
            skLineSegment(sketch, "E27.16.18.0", {"start": v(399.8, 120) * mm, "end": v(398.8, 120) * mm});
            skLineSegment(sketch, "E27.19.18.0", {"start": v(397.8, 135) * mm, "end": v(396.8, 135) * mm});
            skLineSegment(sketch, "E27.22.18.0", {"start": v(398.8, 90) * mm, "end": v(399.8, 90) * mm});
            skLineSegment(sketch, "E27.0.18.1", {"start": v(399.8, 52.5) * mm, "end": v(399.8, 82.5) * mm});
            skLineSegment(sketch, "E27.3.18.1", {"start": v(396.8, 97.5) * mm, "end": v(396.8, 67.5) * mm});
            skPoint(sketch, "E27.6.18.1", {"position": v(396.8, 82.5) * mm});
            skLineSegment(sketch, "E27.7.18.1", {"start": v(397.8, 67.5) * mm, "end": v(397.8, 97.5) * mm});
            skLineSegment(sketch, "E27.10.18.1", {"start": v(398.8, 82.5) * mm, "end": v(398.8, 52.5) * mm});
            skLineSegment(sketch, "E27.13.18.1", {"start": v(396.8, 67.5) * mm, "end": v(397.8, 67.5) * mm});
            skLineSegment(sketch, "E27.16.18.1", {"start": v(399.8, 82.5) * mm, "end": v(398.8, 82.5) * mm});
            skLineSegment(sketch, "E27.19.18.1", {"start": v(397.8, 97.5) * mm, "end": v(396.8, 97.5) * mm});
            skLineSegment(sketch, "E27.22.18.1", {"start": v(398.8, 52.5) * mm, "end": v(399.8, 52.5) * mm});
            skLineSegment(sketch, "E27.0.18.2", {"start": v(399.8, 15) * mm, "end": v(399.8, 45) * mm});
            skLineSegment(sketch, "E27.3.18.2", {"start": v(396.8, 60) * mm, "end": v(396.8, 30) * mm});
            skPoint(sketch, "E27.6.18.2", {"position": v(396.8, 45) * mm});
            skLineSegment(sketch, "E27.7.18.2", {"start": v(397.8, 30) * mm, "end": v(397.8, 60) * mm});
            skLineSegment(sketch, "E27.10.18.2", {"start": v(398.8, 45) * mm, "end": v(398.8, 15) * mm});
            skLineSegment(sketch, "E27.13.18.2", {"start": v(396.8, 30) * mm, "end": v(397.8, 30) * mm});
            skLineSegment(sketch, "E27.16.18.2", {"start": v(399.8, 45) * mm, "end": v(398.8, 45) * mm});
            skLineSegment(sketch, "E27.19.18.2", {"start": v(397.8, 60) * mm, "end": v(396.8, 60) * mm});
            skLineSegment(sketch, "E27.22.18.2", {"start": v(398.8, 15) * mm, "end": v(399.8, 15) * mm});
            skLineSegment(sketch, "E27.0.18.3", {"start": v(399.8, -22.5) * mm, "end": v(399.8, 7.5) * mm});
            skLineSegment(sketch, "E27.3.18.3", {"start": v(396.8, 22.5) * mm, "end": v(396.8, -7.5) * mm});
            skPoint(sketch, "E27.6.18.3", {"position": v(396.8, 7.5) * mm});
            skLineSegment(sketch, "E27.7.18.3", {"start": v(397.8, -7.5) * mm, "end": v(397.8, 22.5) * mm});
            skLineSegment(sketch, "E27.10.18.3", {"start": v(398.8, 7.5) * mm, "end": v(398.8, -22.5) * mm});
            skLineSegment(sketch, "E27.13.18.3", {"start": v(396.8, -7.5) * mm, "end": v(397.8, -7.5) * mm});
            skLineSegment(sketch, "E27.16.18.3", {"start": v(399.8, 7.5) * mm, "end": v(398.8, 7.5) * mm});
            skLineSegment(sketch, "E27.19.18.3", {"start": v(397.8, 22.5) * mm, "end": v(396.8, 22.5) * mm});
            skLineSegment(sketch, "E27.22.18.3", {"start": v(398.8, -22.5) * mm, "end": v(399.8, -22.5) * mm});
            skLineSegment(sketch, "E27.0.19.0", {"start": v(403.8, 90) * mm, "end": v(403.8, 120) * mm});
            skLineSegment(sketch, "E27.3.19.0", {"start": v(400.8, 135) * mm, "end": v(400.8, 105) * mm});
            skPoint(sketch, "E27.6.19.0", {"position": v(400.8, 120) * mm});
            skLineSegment(sketch, "E27.7.19.0", {"start": v(401.8, 105) * mm, "end": v(401.8, 135) * mm});
            skLineSegment(sketch, "E27.10.19.0", {"start": v(402.8, 120) * mm, "end": v(402.8, 90) * mm});
            skLineSegment(sketch, "E27.13.19.0", {"start": v(400.8, 105) * mm, "end": v(401.8, 105) * mm});
            skLineSegment(sketch, "E27.16.19.0", {"start": v(403.8, 120) * mm, "end": v(402.8, 120) * mm});
            skLineSegment(sketch, "E27.19.19.0", {"start": v(401.8, 135) * mm, "end": v(400.8, 135) * mm});
            skLineSegment(sketch, "E27.22.19.0", {"start": v(402.8, 90) * mm, "end": v(403.8, 90) * mm});
            skLineSegment(sketch, "E27.0.19.1", {"start": v(403.8, 52.5) * mm, "end": v(403.8, 82.5) * mm});
            skLineSegment(sketch, "E27.3.19.1", {"start": v(400.8, 97.5) * mm, "end": v(400.8, 67.5) * mm});
            skPoint(sketch, "E27.6.19.1", {"position": v(400.8, 82.5) * mm});
            skLineSegment(sketch, "E27.7.19.1", {"start": v(401.8, 67.5) * mm, "end": v(401.8, 97.5) * mm});
            skLineSegment(sketch, "E27.10.19.1", {"start": v(402.8, 82.5) * mm, "end": v(402.8, 52.5) * mm});
            skLineSegment(sketch, "E27.13.19.1", {"start": v(400.8, 67.5) * mm, "end": v(401.8, 67.5) * mm});
            skLineSegment(sketch, "E27.16.19.1", {"start": v(403.8, 82.5) * mm, "end": v(402.8, 82.5) * mm});
            skLineSegment(sketch, "E27.19.19.1", {"start": v(401.8, 97.5) * mm, "end": v(400.8, 97.5) * mm});
            skLineSegment(sketch, "E27.22.19.1", {"start": v(402.8, 52.5) * mm, "end": v(403.8, 52.5) * mm});
            skLineSegment(sketch, "E27.0.19.2", {"start": v(403.8, 15) * mm, "end": v(403.8, 45) * mm});
            skLineSegment(sketch, "E27.3.19.2", {"start": v(400.8, 60) * mm, "end": v(400.8, 30) * mm});
            skPoint(sketch, "E27.6.19.2", {"position": v(400.8, 45) * mm});
            skLineSegment(sketch, "E27.7.19.2", {"start": v(401.8, 30) * mm, "end": v(401.8, 60) * mm});
            skLineSegment(sketch, "E27.10.19.2", {"start": v(402.8, 45) * mm, "end": v(402.8, 15) * mm});
            skLineSegment(sketch, "E27.13.19.2", {"start": v(400.8, 30) * mm, "end": v(401.8, 30) * mm});
            skLineSegment(sketch, "E27.16.19.2", {"start": v(403.8, 45) * mm, "end": v(402.8, 45) * mm});
            skLineSegment(sketch, "E27.19.19.2", {"start": v(401.8, 60) * mm, "end": v(400.8, 60) * mm});
            skLineSegment(sketch, "E27.22.19.2", {"start": v(402.8, 15) * mm, "end": v(403.8, 15) * mm});
            skLineSegment(sketch, "E27.0.19.3", {"start": v(403.8, -22.5) * mm, "end": v(403.8, 7.5) * mm});
            skLineSegment(sketch, "E27.3.19.3", {"start": v(400.8, 22.5) * mm, "end": v(400.8, -7.5) * mm});
            skPoint(sketch, "E27.6.19.3", {"position": v(400.8, 7.5) * mm});
            skLineSegment(sketch, "E27.7.19.3", {"start": v(401.8, -7.5) * mm, "end": v(401.8, 22.5) * mm});
            skLineSegment(sketch, "E27.10.19.3", {"start": v(402.8, 7.5) * mm, "end": v(402.8, -22.5) * mm});
            skLineSegment(sketch, "E27.13.19.3", {"start": v(400.8, -7.5) * mm, "end": v(401.8, -7.5) * mm});
            skLineSegment(sketch, "E27.16.19.3", {"start": v(403.8, 7.5) * mm, "end": v(402.8, 7.5) * mm});
            skLineSegment(sketch, "E27.19.19.3", {"start": v(401.8, 22.5) * mm, "end": v(400.8, 22.5) * mm});
            skLineSegment(sketch, "E27.22.19.3", {"start": v(402.8, -22.5) * mm, "end": v(403.8, -22.5) * mm});
            skLineSegment(sketch, "E27.0.20.0", {"start": v(407.8, 90) * mm, "end": v(407.8, 120) * mm});
            skLineSegment(sketch, "E27.3.20.0", {"start": v(404.8, 135) * mm, "end": v(404.8, 105) * mm});
            skPoint(sketch, "E27.6.20.0", {"position": v(404.8, 120) * mm});
            skLineSegment(sketch, "E27.7.20.0", {"start": v(405.8, 105) * mm, "end": v(405.8, 135) * mm});
            skLineSegment(sketch, "E27.10.20.0", {"start": v(406.8, 120) * mm, "end": v(406.8, 90) * mm});
            skLineSegment(sketch, "E27.13.20.0", {"start": v(404.8, 105) * mm, "end": v(405.8, 105) * mm});
            skLineSegment(sketch, "E27.16.20.0", {"start": v(407.8, 120) * mm, "end": v(406.8, 120) * mm});
            skLineSegment(sketch, "E27.19.20.0", {"start": v(405.8, 135) * mm, "end": v(404.8, 135) * mm});
            skLineSegment(sketch, "E27.22.20.0", {"start": v(406.8, 90) * mm, "end": v(407.8, 90) * mm});
            skLineSegment(sketch, "E27.0.20.1", {"start": v(407.8, 52.5) * mm, "end": v(407.8, 82.5) * mm});
            skLineSegment(sketch, "E27.3.20.1", {"start": v(404.8, 97.5) * mm, "end": v(404.8, 67.5) * mm});
            skPoint(sketch, "E27.6.20.1", {"position": v(404.8, 82.5) * mm});
            skLineSegment(sketch, "E27.7.20.1", {"start": v(405.8, 67.5) * mm, "end": v(405.8, 97.5) * mm});
            skLineSegment(sketch, "E27.10.20.1", {"start": v(406.8, 82.5) * mm, "end": v(406.8, 52.5) * mm});
            skLineSegment(sketch, "E27.13.20.1", {"start": v(404.8, 67.5) * mm, "end": v(405.8, 67.5) * mm});
            skLineSegment(sketch, "E27.16.20.1", {"start": v(407.8, 82.5) * mm, "end": v(406.8, 82.5) * mm});
            skLineSegment(sketch, "E27.19.20.1", {"start": v(405.8, 97.5) * mm, "end": v(404.8, 97.5) * mm});
            skLineSegment(sketch, "E27.22.20.1", {"start": v(406.8, 52.5) * mm, "end": v(407.8, 52.5) * mm});
            skLineSegment(sketch, "E27.0.20.2", {"start": v(407.8, 15) * mm, "end": v(407.8, 45) * mm});
            skLineSegment(sketch, "E27.3.20.2", {"start": v(404.8, 60) * mm, "end": v(404.8, 30) * mm});
            skPoint(sketch, "E27.6.20.2", {"position": v(404.8, 45) * mm});
            skLineSegment(sketch, "E27.7.20.2", {"start": v(405.8, 30) * mm, "end": v(405.8, 60) * mm});
            skLineSegment(sketch, "E27.10.20.2", {"start": v(406.8, 45) * mm, "end": v(406.8, 15) * mm});
            skLineSegment(sketch, "E27.13.20.2", {"start": v(404.8, 30) * mm, "end": v(405.8, 30) * mm});
            skLineSegment(sketch, "E27.16.20.2", {"start": v(407.8, 45) * mm, "end": v(406.8, 45) * mm});
            skLineSegment(sketch, "E27.19.20.2", {"start": v(405.8, 60) * mm, "end": v(404.8, 60) * mm});
            skLineSegment(sketch, "E27.22.20.2", {"start": v(406.8, 15) * mm, "end": v(407.8, 15) * mm});
            skLineSegment(sketch, "E27.0.20.3", {"start": v(407.8, -22.5) * mm, "end": v(407.8, 7.5) * mm});
            skLineSegment(sketch, "E27.3.20.3", {"start": v(404.8, 22.5) * mm, "end": v(404.8, -7.5) * mm});
            skPoint(sketch, "E27.6.20.3", {"position": v(404.8, 7.5) * mm});
            skLineSegment(sketch, "E27.7.20.3", {"start": v(405.8, -7.5) * mm, "end": v(405.8, 22.5) * mm});
            skLineSegment(sketch, "E27.10.20.3", {"start": v(406.8, 7.5) * mm, "end": v(406.8, -22.5) * mm});
            skLineSegment(sketch, "E27.13.20.3", {"start": v(404.8, -7.5) * mm, "end": v(405.8, -7.5) * mm});
            skLineSegment(sketch, "E27.16.20.3", {"start": v(407.8, 7.5) * mm, "end": v(406.8, 7.5) * mm});
            skLineSegment(sketch, "E27.19.20.3", {"start": v(405.8, 22.5) * mm, "end": v(404.8, 22.5) * mm});
            skLineSegment(sketch, "E27.22.20.3", {"start": v(406.8, -22.5) * mm, "end": v(407.8, -22.5) * mm});
            skLineSegment(sketch, "E27.0.21.0", {"start": v(411.8, 90) * mm, "end": v(411.8, 120) * mm});
            skLineSegment(sketch, "E27.3.21.0", {"start": v(408.8, 135) * mm, "end": v(408.8, 105) * mm});
            skPoint(sketch, "E27.6.21.0", {"position": v(408.8, 120) * mm});
            skLineSegment(sketch, "E27.7.21.0", {"start": v(409.8, 105) * mm, "end": v(409.8, 135) * mm});
            skLineSegment(sketch, "E27.10.21.0", {"start": v(410.8, 120) * mm, "end": v(410.8, 90) * mm});
            skLineSegment(sketch, "E27.13.21.0", {"start": v(408.8, 105) * mm, "end": v(409.8, 105) * mm});
            skLineSegment(sketch, "E27.16.21.0", {"start": v(411.8, 120) * mm, "end": v(410.8, 120) * mm});
            skLineSegment(sketch, "E27.19.21.0", {"start": v(409.8, 135) * mm, "end": v(408.8, 135) * mm});
            skLineSegment(sketch, "E27.22.21.0", {"start": v(410.8, 90) * mm, "end": v(411.8, 90) * mm});
            skLineSegment(sketch, "E27.0.21.1", {"start": v(411.8, 52.5) * mm, "end": v(411.8, 82.5) * mm});
            skLineSegment(sketch, "E27.3.21.1", {"start": v(408.8, 97.5) * mm, "end": v(408.8, 67.5) * mm});
            skPoint(sketch, "E27.6.21.1", {"position": v(408.8, 82.5) * mm});
            skLineSegment(sketch, "E27.7.21.1", {"start": v(409.8, 67.5) * mm, "end": v(409.8, 97.5) * mm});
            skLineSegment(sketch, "E27.10.21.1", {"start": v(410.8, 82.5) * mm, "end": v(410.8, 52.5) * mm});
            skLineSegment(sketch, "E27.13.21.1", {"start": v(408.8, 67.5) * mm, "end": v(409.8, 67.5) * mm});
            skLineSegment(sketch, "E27.16.21.1", {"start": v(411.8, 82.5) * mm, "end": v(410.8, 82.5) * mm});
            skLineSegment(sketch, "E27.19.21.1", {"start": v(409.8, 97.5) * mm, "end": v(408.8, 97.5) * mm});
            skLineSegment(sketch, "E27.22.21.1", {"start": v(410.8, 52.5) * mm, "end": v(411.8, 52.5) * mm});
            skLineSegment(sketch, "E27.0.21.2", {"start": v(411.8, 15) * mm, "end": v(411.8, 45) * mm});
            skLineSegment(sketch, "E27.3.21.2", {"start": v(408.8, 60) * mm, "end": v(408.8, 30) * mm});
            skPoint(sketch, "E27.6.21.2", {"position": v(408.8, 45) * mm});
            skLineSegment(sketch, "E27.7.21.2", {"start": v(409.8, 30) * mm, "end": v(409.8, 60) * mm});
            skLineSegment(sketch, "E27.10.21.2", {"start": v(410.8, 45) * mm, "end": v(410.8, 15) * mm});
            skLineSegment(sketch, "E27.13.21.2", {"start": v(408.8, 30) * mm, "end": v(409.8, 30) * mm});
            skLineSegment(sketch, "E27.16.21.2", {"start": v(411.8, 45) * mm, "end": v(410.8, 45) * mm});
            skLineSegment(sketch, "E27.19.21.2", {"start": v(409.8, 60) * mm, "end": v(408.8, 60) * mm});
            skLineSegment(sketch, "E27.22.21.2", {"start": v(410.8, 15) * mm, "end": v(411.8, 15) * mm});
            skLineSegment(sketch, "E27.0.21.3", {"start": v(411.8, -22.5) * mm, "end": v(411.8, 7.5) * mm});
            skLineSegment(sketch, "E27.3.21.3", {"start": v(408.8, 22.5) * mm, "end": v(408.8, -7.5) * mm});
            skPoint(sketch, "E27.6.21.3", {"position": v(408.8, 7.5) * mm});
            skLineSegment(sketch, "E27.7.21.3", {"start": v(409.8, -7.5) * mm, "end": v(409.8, 22.5) * mm});
            skLineSegment(sketch, "E27.10.21.3", {"start": v(410.8, 7.5) * mm, "end": v(410.8, -22.5) * mm});
            skLineSegment(sketch, "E27.13.21.3", {"start": v(408.8, -7.5) * mm, "end": v(409.8, -7.5) * mm});
            skLineSegment(sketch, "E27.16.21.3", {"start": v(411.8, 7.5) * mm, "end": v(410.8, 7.5) * mm});
            skLineSegment(sketch, "E27.19.21.3", {"start": v(409.8, 22.5) * mm, "end": v(408.8, 22.5) * mm});
            skLineSegment(sketch, "E27.22.21.3", {"start": v(410.8, -22.5) * mm, "end": v(411.8, -22.5) * mm});
            skLineSegment(sketch, "E27.0.22.0", {"start": v(415.8, 90) * mm, "end": v(415.8, 120) * mm});
            skLineSegment(sketch, "E27.3.22.0", {"start": v(412.8, 135) * mm, "end": v(412.8, 105) * mm});
            skPoint(sketch, "E27.6.22.0", {"position": v(412.8, 120) * mm});
            skLineSegment(sketch, "E27.7.22.0", {"start": v(413.8, 105) * mm, "end": v(413.8, 135) * mm});
            skLineSegment(sketch, "E27.10.22.0", {"start": v(414.8, 120) * mm, "end": v(414.8, 90) * mm});
            skLineSegment(sketch, "E27.13.22.0", {"start": v(412.8, 105) * mm, "end": v(413.8, 105) * mm});
            skLineSegment(sketch, "E27.16.22.0", {"start": v(415.8, 120) * mm, "end": v(414.8, 120) * mm});
            skLineSegment(sketch, "E27.19.22.0", {"start": v(413.8, 135) * mm, "end": v(412.8, 135) * mm});
            skLineSegment(sketch, "E27.22.22.0", {"start": v(414.8, 90) * mm, "end": v(415.8, 90) * mm});
            skLineSegment(sketch, "E27.0.22.1", {"start": v(415.8, 52.5) * mm, "end": v(415.8, 82.5) * mm});
            skLineSegment(sketch, "E27.3.22.1", {"start": v(412.8, 97.5) * mm, "end": v(412.8, 67.5) * mm});
            skPoint(sketch, "E27.6.22.1", {"position": v(412.8, 82.5) * mm});
            skLineSegment(sketch, "E27.7.22.1", {"start": v(413.8, 67.5) * mm, "end": v(413.8, 97.5) * mm});
            skLineSegment(sketch, "E27.10.22.1", {"start": v(414.8, 82.5) * mm, "end": v(414.8, 52.5) * mm});
            skLineSegment(sketch, "E27.13.22.1", {"start": v(412.8, 67.5) * mm, "end": v(413.8, 67.5) * mm});
            skLineSegment(sketch, "E27.16.22.1", {"start": v(415.8, 82.5) * mm, "end": v(414.8, 82.5) * mm});
            skLineSegment(sketch, "E27.19.22.1", {"start": v(413.8, 97.5) * mm, "end": v(412.8, 97.5) * mm});
            skLineSegment(sketch, "E27.22.22.1", {"start": v(414.8, 52.5) * mm, "end": v(415.8, 52.5) * mm});
            skLineSegment(sketch, "E27.0.22.2", {"start": v(415.8, 15) * mm, "end": v(415.8, 45) * mm});
            skLineSegment(sketch, "E27.3.22.2", {"start": v(412.8, 60) * mm, "end": v(412.8, 30) * mm});
            skPoint(sketch, "E27.6.22.2", {"position": v(412.8, 45) * mm});
            skLineSegment(sketch, "E27.7.22.2", {"start": v(413.8, 30) * mm, "end": v(413.8, 60) * mm});
            skLineSegment(sketch, "E27.10.22.2", {"start": v(414.8, 45) * mm, "end": v(414.8, 15) * mm});
            skLineSegment(sketch, "E27.13.22.2", {"start": v(412.8, 30) * mm, "end": v(413.8, 30) * mm});
            skLineSegment(sketch, "E27.16.22.2", {"start": v(415.8, 45) * mm, "end": v(414.8, 45) * mm});
            skLineSegment(sketch, "E27.19.22.2", {"start": v(413.8, 60) * mm, "end": v(412.8, 60) * mm});
            skLineSegment(sketch, "E27.22.22.2", {"start": v(414.8, 15) * mm, "end": v(415.8, 15) * mm});
            skLineSegment(sketch, "E27.0.22.3", {"start": v(415.8, -22.5) * mm, "end": v(415.8, 7.5) * mm});
            skLineSegment(sketch, "E27.3.22.3", {"start": v(412.8, 22.5) * mm, "end": v(412.8, -7.5) * mm});
            skPoint(sketch, "E27.6.22.3", {"position": v(412.8, 7.5) * mm});
            skLineSegment(sketch, "E27.7.22.3", {"start": v(413.8, -7.5) * mm, "end": v(413.8, 22.5) * mm});
            skLineSegment(sketch, "E27.10.22.3", {"start": v(414.8, 7.5) * mm, "end": v(414.8, -22.5) * mm});
            skLineSegment(sketch, "E27.13.22.3", {"start": v(412.8, -7.5) * mm, "end": v(413.8, -7.5) * mm});
            skLineSegment(sketch, "E27.16.22.3", {"start": v(415.8, 7.5) * mm, "end": v(414.8, 7.5) * mm});
            skLineSegment(sketch, "E27.19.22.3", {"start": v(413.8, 22.5) * mm, "end": v(412.8, 22.5) * mm});
            skLineSegment(sketch, "E27.22.22.3", {"start": v(414.8, -22.5) * mm, "end": v(415.8, -22.5) * mm});
            skLineSegment(sketch, "E27.0.23.0", {"start": v(419.8, 90) * mm, "end": v(419.8, 120) * mm});
            skLineSegment(sketch, "E27.3.23.0", {"start": v(416.8, 135) * mm, "end": v(416.8, 105) * mm});
            skPoint(sketch, "E27.6.23.0", {"position": v(416.8, 120) * mm});
            skLineSegment(sketch, "E27.7.23.0", {"start": v(417.8, 105) * mm, "end": v(417.8, 135) * mm});
            skLineSegment(sketch, "E27.10.23.0", {"start": v(418.8, 120) * mm, "end": v(418.8, 90) * mm});
            skLineSegment(sketch, "E27.13.23.0", {"start": v(416.8, 105) * mm, "end": v(417.8, 105) * mm});
            skLineSegment(sketch, "E27.16.23.0", {"start": v(419.8, 120) * mm, "end": v(418.8, 120) * mm});
            skLineSegment(sketch, "E27.19.23.0", {"start": v(417.8, 135) * mm, "end": v(416.8, 135) * mm});
            skLineSegment(sketch, "E27.22.23.0", {"start": v(418.8, 90) * mm, "end": v(419.8, 90) * mm});
            skLineSegment(sketch, "E27.0.23.1", {"start": v(419.8, 52.5) * mm, "end": v(419.8, 82.5) * mm});
            skLineSegment(sketch, "E27.3.23.1", {"start": v(416.8, 97.5) * mm, "end": v(416.8, 67.5) * mm});
            skPoint(sketch, "E27.6.23.1", {"position": v(416.8, 82.5) * mm});
            skLineSegment(sketch, "E27.7.23.1", {"start": v(417.8, 67.5) * mm, "end": v(417.8, 97.5) * mm});
            skLineSegment(sketch, "E27.10.23.1", {"start": v(418.8, 82.5) * mm, "end": v(418.8, 52.5) * mm});
            skLineSegment(sketch, "E27.13.23.1", {"start": v(416.8, 67.5) * mm, "end": v(417.8, 67.5) * mm});
            skLineSegment(sketch, "E27.16.23.1", {"start": v(419.8, 82.5) * mm, "end": v(418.8, 82.5) * mm});
            skLineSegment(sketch, "E27.19.23.1", {"start": v(417.8, 97.5) * mm, "end": v(416.8, 97.5) * mm});
            skLineSegment(sketch, "E27.22.23.1", {"start": v(418.8, 52.5) * mm, "end": v(419.8, 52.5) * mm});
            skLineSegment(sketch, "E27.0.23.2", {"start": v(419.8, 15) * mm, "end": v(419.8, 45) * mm});
            skLineSegment(sketch, "E27.3.23.2", {"start": v(416.8, 60) * mm, "end": v(416.8, 30) * mm});
            skPoint(sketch, "E27.6.23.2", {"position": v(416.8, 45) * mm});
            skLineSegment(sketch, "E27.7.23.2", {"start": v(417.8, 30) * mm, "end": v(417.8, 60) * mm});
            skLineSegment(sketch, "E27.10.23.2", {"start": v(418.8, 45) * mm, "end": v(418.8, 15) * mm});
            skLineSegment(sketch, "E27.13.23.2", {"start": v(416.8, 30) * mm, "end": v(417.8, 30) * mm});
            skLineSegment(sketch, "E27.16.23.2", {"start": v(419.8, 45) * mm, "end": v(418.8, 45) * mm});
            skLineSegment(sketch, "E27.19.23.2", {"start": v(417.8, 60) * mm, "end": v(416.8, 60) * mm});
            skLineSegment(sketch, "E27.22.23.2", {"start": v(418.8, 15) * mm, "end": v(419.8, 15) * mm});
            skLineSegment(sketch, "E27.0.23.3", {"start": v(419.8, -22.5) * mm, "end": v(419.8, 7.5) * mm});
            skLineSegment(sketch, "E27.3.23.3", {"start": v(416.8, 22.5) * mm, "end": v(416.8, -7.5) * mm});
            skPoint(sketch, "E27.6.23.3", {"position": v(416.8, 7.5) * mm});
            skLineSegment(sketch, "E27.7.23.3", {"start": v(417.8, -7.5) * mm, "end": v(417.8, 22.5) * mm});
            skLineSegment(sketch, "E27.10.23.3", {"start": v(418.8, 7.5) * mm, "end": v(418.8, -22.5) * mm});
            skLineSegment(sketch, "E27.13.23.3", {"start": v(416.8, -7.5) * mm, "end": v(417.8, -7.5) * mm});
            skLineSegment(sketch, "E27.16.23.3", {"start": v(419.8, 7.5) * mm, "end": v(418.8, 7.5) * mm});
            skLineSegment(sketch, "E27.19.23.3", {"start": v(417.8, 22.5) * mm, "end": v(416.8, 22.5) * mm});
            skLineSegment(sketch, "E27.22.23.3", {"start": v(418.8, -22.5) * mm, "end": v(419.8, -22.5) * mm});
            skLineSegment(sketch, "E27.0.24.0", {"start": v(423.8, 90) * mm, "end": v(423.8, 120) * mm});
            skLineSegment(sketch, "E27.3.24.0", {"start": v(420.8, 135) * mm, "end": v(420.8, 105) * mm});
            skPoint(sketch, "E27.6.24.0", {"position": v(420.8, 120) * mm});
            skLineSegment(sketch, "E27.7.24.0", {"start": v(421.8, 105) * mm, "end": v(421.8, 135) * mm});
            skLineSegment(sketch, "E27.10.24.0", {"start": v(422.8, 120) * mm, "end": v(422.8, 90) * mm});
            skLineSegment(sketch, "E27.13.24.0", {"start": v(420.8, 105) * mm, "end": v(421.8, 105) * mm});
            skLineSegment(sketch, "E27.16.24.0", {"start": v(423.8, 120) * mm, "end": v(422.8, 120) * mm});
            skLineSegment(sketch, "E27.19.24.0", {"start": v(421.8, 135) * mm, "end": v(420.8, 135) * mm});
            skLineSegment(sketch, "E27.22.24.0", {"start": v(422.8, 90) * mm, "end": v(423.8, 90) * mm});
            skLineSegment(sketch, "E27.0.24.1", {"start": v(423.8, 52.5) * mm, "end": v(423.8, 82.5) * mm});
            skLineSegment(sketch, "E27.3.24.1", {"start": v(420.8, 97.5) * mm, "end": v(420.8, 67.5) * mm});
            skPoint(sketch, "E27.6.24.1", {"position": v(420.8, 82.5) * mm});
            skLineSegment(sketch, "E27.7.24.1", {"start": v(421.8, 67.5) * mm, "end": v(421.8, 97.5) * mm});
            skLineSegment(sketch, "E27.10.24.1", {"start": v(422.8, 82.5) * mm, "end": v(422.8, 52.5) * mm});
            skLineSegment(sketch, "E27.13.24.1", {"start": v(420.8, 67.5) * mm, "end": v(421.8, 67.5) * mm});
            skLineSegment(sketch, "E27.16.24.1", {"start": v(423.8, 82.5) * mm, "end": v(422.8, 82.5) * mm});
            skLineSegment(sketch, "E27.19.24.1", {"start": v(421.8, 97.5) * mm, "end": v(420.8, 97.5) * mm});
            skLineSegment(sketch, "E27.22.24.1", {"start": v(422.8, 52.5) * mm, "end": v(423.8, 52.5) * mm});
            skLineSegment(sketch, "E27.0.24.2", {"start": v(423.8, 15) * mm, "end": v(423.8, 45) * mm});
            skLineSegment(sketch, "E27.3.24.2", {"start": v(420.8, 60) * mm, "end": v(420.8, 30) * mm});
            skPoint(sketch, "E27.6.24.2", {"position": v(420.8, 45) * mm});
            skLineSegment(sketch, "E27.7.24.2", {"start": v(421.8, 30) * mm, "end": v(421.8, 60) * mm});
            skLineSegment(sketch, "E27.10.24.2", {"start": v(422.8, 45) * mm, "end": v(422.8, 15) * mm});
            skLineSegment(sketch, "E27.13.24.2", {"start": v(420.8, 30) * mm, "end": v(421.8, 30) * mm});
            skLineSegment(sketch, "E27.16.24.2", {"start": v(423.8, 45) * mm, "end": v(422.8, 45) * mm});
            skLineSegment(sketch, "E27.19.24.2", {"start": v(421.8, 60) * mm, "end": v(420.8, 60) * mm});
            skLineSegment(sketch, "E27.22.24.2", {"start": v(422.8, 15) * mm, "end": v(423.8, 15) * mm});
            skLineSegment(sketch, "E27.0.24.3", {"start": v(423.8, -22.5) * mm, "end": v(423.8, 7.5) * mm});
            skLineSegment(sketch, "E27.3.24.3", {"start": v(420.8, 22.5) * mm, "end": v(420.8, -7.5) * mm});
            skPoint(sketch, "E27.6.24.3", {"position": v(420.8, 7.5) * mm});
            skLineSegment(sketch, "E27.7.24.3", {"start": v(421.8, -7.5) * mm, "end": v(421.8, 22.5) * mm});
            skLineSegment(sketch, "E27.10.24.3", {"start": v(422.8, 7.5) * mm, "end": v(422.8, -22.5) * mm});
            skLineSegment(sketch, "E27.13.24.3", {"start": v(420.8, -7.5) * mm, "end": v(421.8, -7.5) * mm});
            skLineSegment(sketch, "E27.16.24.3", {"start": v(423.8, 7.5) * mm, "end": v(422.8, 7.5) * mm});
            skLineSegment(sketch, "E27.19.24.3", {"start": v(421.8, 22.5) * mm, "end": v(420.8, 22.5) * mm});
            skLineSegment(sketch, "E27.22.24.3", {"start": v(422.8, -22.5) * mm, "end": v(423.8, -22.5) * mm});
            skLineSegment(sketch, "E27.0.25.0", {"start": v(427.8, 90) * mm, "end": v(427.8, 120) * mm});
            skLineSegment(sketch, "E27.3.25.0", {"start": v(424.8, 135) * mm, "end": v(424.8, 105) * mm});
            skPoint(sketch, "E27.6.25.0", {"position": v(424.8, 120) * mm});
            skLineSegment(sketch, "E27.7.25.0", {"start": v(425.8, 105) * mm, "end": v(425.8, 135) * mm});
            skLineSegment(sketch, "E27.10.25.0", {"start": v(426.8, 120) * mm, "end": v(426.8, 90) * mm});
            skLineSegment(sketch, "E27.13.25.0", {"start": v(424.8, 105) * mm, "end": v(425.8, 105) * mm});
            skLineSegment(sketch, "E27.16.25.0", {"start": v(427.8, 120) * mm, "end": v(426.8, 120) * mm});
            skLineSegment(sketch, "E27.19.25.0", {"start": v(425.8, 135) * mm, "end": v(424.8, 135) * mm});
            skLineSegment(sketch, "E27.22.25.0", {"start": v(426.8, 90) * mm, "end": v(427.8, 90) * mm});
            skLineSegment(sketch, "E27.0.25.1", {"start": v(427.8, 52.5) * mm, "end": v(427.8, 82.5) * mm});
            skLineSegment(sketch, "E27.3.25.1", {"start": v(424.8, 97.5) * mm, "end": v(424.8, 67.5) * mm});
            skPoint(sketch, "E27.6.25.1", {"position": v(424.8, 82.5) * mm});
            skLineSegment(sketch, "E27.7.25.1", {"start": v(425.8, 67.5) * mm, "end": v(425.8, 97.5) * mm});
            skLineSegment(sketch, "E27.10.25.1", {"start": v(426.8, 82.5) * mm, "end": v(426.8, 52.5) * mm});
            skLineSegment(sketch, "E27.13.25.1", {"start": v(424.8, 67.5) * mm, "end": v(425.8, 67.5) * mm});
            skLineSegment(sketch, "E27.16.25.1", {"start": v(427.8, 82.5) * mm, "end": v(426.8, 82.5) * mm});
            skLineSegment(sketch, "E27.19.25.1", {"start": v(425.8, 97.5) * mm, "end": v(424.8, 97.5) * mm});
            skLineSegment(sketch, "E27.22.25.1", {"start": v(426.8, 52.5) * mm, "end": v(427.8, 52.5) * mm});
            skLineSegment(sketch, "E27.0.25.2", {"start": v(427.8, 15) * mm, "end": v(427.8, 45) * mm});
            skLineSegment(sketch, "E27.3.25.2", {"start": v(424.8, 60) * mm, "end": v(424.8, 30) * mm});
            skPoint(sketch, "E27.6.25.2", {"position": v(424.8, 45) * mm});
            skLineSegment(sketch, "E27.7.25.2", {"start": v(425.8, 30) * mm, "end": v(425.8, 60) * mm});
            skLineSegment(sketch, "E27.10.25.2", {"start": v(426.8, 45) * mm, "end": v(426.8, 15) * mm});
            skLineSegment(sketch, "E27.13.25.2", {"start": v(424.8, 30) * mm, "end": v(425.8, 30) * mm});
            skLineSegment(sketch, "E27.16.25.2", {"start": v(427.8, 45) * mm, "end": v(426.8, 45) * mm});
            skLineSegment(sketch, "E27.19.25.2", {"start": v(425.8, 60) * mm, "end": v(424.8, 60) * mm});
            skLineSegment(sketch, "E27.22.25.2", {"start": v(426.8, 15) * mm, "end": v(427.8, 15) * mm});
            skLineSegment(sketch, "E27.0.25.3", {"start": v(427.8, -22.5) * mm, "end": v(427.8, 7.5) * mm});
            skLineSegment(sketch, "E27.3.25.3", {"start": v(424.8, 22.5) * mm, "end": v(424.8, -7.5) * mm});
            skPoint(sketch, "E27.6.25.3", {"position": v(424.8, 7.5) * mm});
            skLineSegment(sketch, "E27.7.25.3", {"start": v(425.8, -7.5) * mm, "end": v(425.8, 22.5) * mm});
            skLineSegment(sketch, "E27.10.25.3", {"start": v(426.8, 7.5) * mm, "end": v(426.8, -22.5) * mm});
            skLineSegment(sketch, "E27.13.25.3", {"start": v(424.8, -7.5) * mm, "end": v(425.8, -7.5) * mm});
            skLineSegment(sketch, "E27.16.25.3", {"start": v(427.8, 7.5) * mm, "end": v(426.8, 7.5) * mm});
            skLineSegment(sketch, "E27.19.25.3", {"start": v(425.8, 22.5) * mm, "end": v(424.8, 22.5) * mm});
            skLineSegment(sketch, "E27.22.25.3", {"start": v(426.8, -22.5) * mm, "end": v(427.8, -22.5) * mm});
            skLineSegment(sketch, "E27.0.26.0", {"start": v(431.8, 90) * mm, "end": v(431.8, 120) * mm});
            skLineSegment(sketch, "E27.3.26.0", {"start": v(428.8, 135) * mm, "end": v(428.8, 105) * mm});
            skPoint(sketch, "E27.6.26.0", {"position": v(428.8, 120) * mm});
            skLineSegment(sketch, "E27.7.26.0", {"start": v(429.8, 105) * mm, "end": v(429.8, 135) * mm});
            skLineSegment(sketch, "E27.10.26.0", {"start": v(430.8, 120) * mm, "end": v(430.8, 90) * mm});
            skLineSegment(sketch, "E27.13.26.0", {"start": v(428.8, 105) * mm, "end": v(429.8, 105) * mm});
            skLineSegment(sketch, "E27.16.26.0", {"start": v(431.8, 120) * mm, "end": v(430.8, 120) * mm});
            skLineSegment(sketch, "E27.19.26.0", {"start": v(429.8, 135) * mm, "end": v(428.8, 135) * mm});
            skLineSegment(sketch, "E27.22.26.0", {"start": v(430.8, 90) * mm, "end": v(431.8, 90) * mm});
            skLineSegment(sketch, "E27.0.26.1", {"start": v(431.8, 52.5) * mm, "end": v(431.8, 82.5) * mm});
            skLineSegment(sketch, "E27.3.26.1", {"start": v(428.8, 97.5) * mm, "end": v(428.8, 67.5) * mm});
            skPoint(sketch, "E27.6.26.1", {"position": v(428.8, 82.5) * mm});
            skLineSegment(sketch, "E27.7.26.1", {"start": v(429.8, 67.5) * mm, "end": v(429.8, 97.5) * mm});
            skLineSegment(sketch, "E27.10.26.1", {"start": v(430.8, 82.5) * mm, "end": v(430.8, 52.5) * mm});
            skLineSegment(sketch, "E27.13.26.1", {"start": v(428.8, 67.5) * mm, "end": v(429.8, 67.5) * mm});
            skLineSegment(sketch, "E27.16.26.1", {"start": v(431.8, 82.5) * mm, "end": v(430.8, 82.5) * mm});
            skLineSegment(sketch, "E27.19.26.1", {"start": v(429.8, 97.5) * mm, "end": v(428.8, 97.5) * mm});
            skLineSegment(sketch, "E27.22.26.1", {"start": v(430.8, 52.5) * mm, "end": v(431.8, 52.5) * mm});
            skLineSegment(sketch, "E27.0.26.2", {"start": v(431.8, 15) * mm, "end": v(431.8, 45) * mm});
            skLineSegment(sketch, "E27.3.26.2", {"start": v(428.8, 60) * mm, "end": v(428.8, 30) * mm});
            skPoint(sketch, "E27.6.26.2", {"position": v(428.8, 45) * mm});
            skLineSegment(sketch, "E27.7.26.2", {"start": v(429.8, 30) * mm, "end": v(429.8, 60) * mm});
            skLineSegment(sketch, "E27.10.26.2", {"start": v(430.8, 45) * mm, "end": v(430.8, 15) * mm});
            skLineSegment(sketch, "E27.13.26.2", {"start": v(428.8, 30) * mm, "end": v(429.8, 30) * mm});
            skLineSegment(sketch, "E27.16.26.2", {"start": v(431.8, 45) * mm, "end": v(430.8, 45) * mm});
            skLineSegment(sketch, "E27.19.26.2", {"start": v(429.8, 60) * mm, "end": v(428.8, 60) * mm});
            skLineSegment(sketch, "E27.22.26.2", {"start": v(430.8, 15) * mm, "end": v(431.8, 15) * mm});
            skLineSegment(sketch, "E27.0.26.3", {"start": v(431.8, -22.5) * mm, "end": v(431.8, 7.5) * mm});
            skLineSegment(sketch, "E27.3.26.3", {"start": v(428.8, 22.5) * mm, "end": v(428.8, -7.5) * mm});
            skPoint(sketch, "E27.6.26.3", {"position": v(428.8, 7.5) * mm});
            skLineSegment(sketch, "E27.7.26.3", {"start": v(429.8, -7.5) * mm, "end": v(429.8, 22.5) * mm});
            skLineSegment(sketch, "E27.10.26.3", {"start": v(430.8, 7.5) * mm, "end": v(430.8, -22.5) * mm});
            skLineSegment(sketch, "E27.13.26.3", {"start": v(428.8, -7.5) * mm, "end": v(429.8, -7.5) * mm});
            skLineSegment(sketch, "E27.16.26.3", {"start": v(431.8, 7.5) * mm, "end": v(430.8, 7.5) * mm});
            skLineSegment(sketch, "E27.19.26.3", {"start": v(429.8, 22.5) * mm, "end": v(428.8, 22.5) * mm});
            skLineSegment(sketch, "E27.22.26.3", {"start": v(430.8, -22.5) * mm, "end": v(431.8, -22.5) * mm});
            skLineSegment(sketch, "E27.0.27.0", {"start": v(435.8, 90) * mm, "end": v(435.8, 120) * mm});
            skLineSegment(sketch, "E27.3.27.0", {"start": v(432.8, 135) * mm, "end": v(432.8, 105) * mm});
            skPoint(sketch, "E27.6.27.0", {"position": v(432.8, 120) * mm});
            skLineSegment(sketch, "E27.7.27.0", {"start": v(433.8, 105) * mm, "end": v(433.8, 135) * mm});
            skLineSegment(sketch, "E27.10.27.0", {"start": v(434.8, 120) * mm, "end": v(434.8, 90) * mm});
            skLineSegment(sketch, "E27.13.27.0", {"start": v(432.8, 105) * mm, "end": v(433.8, 105) * mm});
            skLineSegment(sketch, "E27.16.27.0", {"start": v(435.8, 120) * mm, "end": v(434.8, 120) * mm});
            skLineSegment(sketch, "E27.19.27.0", {"start": v(433.8, 135) * mm, "end": v(432.8, 135) * mm});
            skLineSegment(sketch, "E27.22.27.0", {"start": v(434.8, 90) * mm, "end": v(435.8, 90) * mm});
            skLineSegment(sketch, "E27.0.27.1", {"start": v(435.8, 52.5) * mm, "end": v(435.8, 82.5) * mm});
            skLineSegment(sketch, "E27.3.27.1", {"start": v(432.8, 97.5) * mm, "end": v(432.8, 67.5) * mm});
            skPoint(sketch, "E27.6.27.1", {"position": v(432.8, 82.5) * mm});
            skLineSegment(sketch, "E27.7.27.1", {"start": v(433.8, 67.5) * mm, "end": v(433.8, 97.5) * mm});
            skLineSegment(sketch, "E27.10.27.1", {"start": v(434.8, 82.5) * mm, "end": v(434.8, 52.5) * mm});
            skLineSegment(sketch, "E27.13.27.1", {"start": v(432.8, 67.5) * mm, "end": v(433.8, 67.5) * mm});
            skLineSegment(sketch, "E27.16.27.1", {"start": v(435.8, 82.5) * mm, "end": v(434.8, 82.5) * mm});
            skLineSegment(sketch, "E27.19.27.1", {"start": v(433.8, 97.5) * mm, "end": v(432.8, 97.5) * mm});
            skLineSegment(sketch, "E27.22.27.1", {"start": v(434.8, 52.5) * mm, "end": v(435.8, 52.5) * mm});
            skLineSegment(sketch, "E27.0.27.2", {"start": v(435.8, 15) * mm, "end": v(435.8, 45) * mm});
            skLineSegment(sketch, "E27.3.27.2", {"start": v(432.8, 60) * mm, "end": v(432.8, 30) * mm});
            skPoint(sketch, "E27.6.27.2", {"position": v(432.8, 45) * mm});
            skLineSegment(sketch, "E27.7.27.2", {"start": v(433.8, 30) * mm, "end": v(433.8, 60) * mm});
            skLineSegment(sketch, "E27.10.27.2", {"start": v(434.8, 45) * mm, "end": v(434.8, 15) * mm});
            skLineSegment(sketch, "E27.13.27.2", {"start": v(432.8, 30) * mm, "end": v(433.8, 30) * mm});
            skLineSegment(sketch, "E27.16.27.2", {"start": v(435.8, 45) * mm, "end": v(434.8, 45) * mm});
            skLineSegment(sketch, "E27.19.27.2", {"start": v(433.8, 60) * mm, "end": v(432.8, 60) * mm});
            skLineSegment(sketch, "E27.22.27.2", {"start": v(434.8, 15) * mm, "end": v(435.8, 15) * mm});
            skLineSegment(sketch, "E27.0.27.3", {"start": v(435.8, -22.5) * mm, "end": v(435.8, 7.5) * mm});
            skLineSegment(sketch, "E27.3.27.3", {"start": v(432.8, 22.5) * mm, "end": v(432.8, -7.5) * mm});
            skPoint(sketch, "E27.6.27.3", {"position": v(432.8, 7.5) * mm});
            skLineSegment(sketch, "E27.7.27.3", {"start": v(433.8, -7.5) * mm, "end": v(433.8, 22.5) * mm});
            skLineSegment(sketch, "E27.10.27.3", {"start": v(434.8, 7.5) * mm, "end": v(434.8, -22.5) * mm});
            skLineSegment(sketch, "E27.13.27.3", {"start": v(432.8, -7.5) * mm, "end": v(433.8, -7.5) * mm});
            skLineSegment(sketch, "E27.16.27.3", {"start": v(435.8, 7.5) * mm, "end": v(434.8, 7.5) * mm});
            skLineSegment(sketch, "E27.19.27.3", {"start": v(433.8, 22.5) * mm, "end": v(432.8, 22.5) * mm});
            skLineSegment(sketch, "E27.22.27.3", {"start": v(434.8, -22.5) * mm, "end": v(435.8, -22.5) * mm});
            skLineSegment(sketch, "E27.0.28.0", {"start": v(439.8, 90) * mm, "end": v(439.8, 120) * mm});
            skLineSegment(sketch, "E27.3.28.0", {"start": v(436.8, 135) * mm, "end": v(436.8, 105) * mm});
            skPoint(sketch, "E27.6.28.0", {"position": v(436.8, 120) * mm});
            skLineSegment(sketch, "E27.7.28.0", {"start": v(437.8, 105) * mm, "end": v(437.8, 135) * mm});
            skLineSegment(sketch, "E27.10.28.0", {"start": v(438.8, 120) * mm, "end": v(438.8, 90) * mm});
            skLineSegment(sketch, "E27.13.28.0", {"start": v(436.8, 105) * mm, "end": v(437.8, 105) * mm});
            skLineSegment(sketch, "E27.16.28.0", {"start": v(439.8, 120) * mm, "end": v(438.8, 120) * mm});
            skLineSegment(sketch, "E27.19.28.0", {"start": v(437.8, 135) * mm, "end": v(436.8, 135) * mm});
            skLineSegment(sketch, "E27.22.28.0", {"start": v(438.8, 90) * mm, "end": v(439.8, 90) * mm});
            skLineSegment(sketch, "E27.0.28.1", {"start": v(439.8, 52.5) * mm, "end": v(439.8, 82.5) * mm});
            skLineSegment(sketch, "E27.3.28.1", {"start": v(436.8, 97.5) * mm, "end": v(436.8, 67.5) * mm});
            skPoint(sketch, "E27.6.28.1", {"position": v(436.8, 82.5) * mm});
            skLineSegment(sketch, "E27.7.28.1", {"start": v(437.8, 67.5) * mm, "end": v(437.8, 97.5) * mm});
            skLineSegment(sketch, "E27.10.28.1", {"start": v(438.8, 82.5) * mm, "end": v(438.8, 52.5) * mm});
            skLineSegment(sketch, "E27.13.28.1", {"start": v(436.8, 67.5) * mm, "end": v(437.8, 67.5) * mm});
            skLineSegment(sketch, "E27.16.28.1", {"start": v(439.8, 82.5) * mm, "end": v(438.8, 82.5) * mm});
            skLineSegment(sketch, "E27.19.28.1", {"start": v(437.8, 97.5) * mm, "end": v(436.8, 97.5) * mm});
            skLineSegment(sketch, "E27.22.28.1", {"start": v(438.8, 52.5) * mm, "end": v(439.8, 52.5) * mm});
            skLineSegment(sketch, "E27.0.28.2", {"start": v(439.8, 15) * mm, "end": v(439.8, 45) * mm});
            skLineSegment(sketch, "E27.3.28.2", {"start": v(436.8, 60) * mm, "end": v(436.8, 30) * mm});
            skPoint(sketch, "E27.6.28.2", {"position": v(436.8, 45) * mm});
            skLineSegment(sketch, "E27.7.28.2", {"start": v(437.8, 30) * mm, "end": v(437.8, 60) * mm});
            skLineSegment(sketch, "E27.10.28.2", {"start": v(438.8, 45) * mm, "end": v(438.8, 15) * mm});
            skLineSegment(sketch, "E27.13.28.2", {"start": v(436.8, 30) * mm, "end": v(437.8, 30) * mm});
            skLineSegment(sketch, "E27.16.28.2", {"start": v(439.8, 45) * mm, "end": v(438.8, 45) * mm});
            skLineSegment(sketch, "E27.19.28.2", {"start": v(437.8, 60) * mm, "end": v(436.8, 60) * mm});
            skLineSegment(sketch, "E27.22.28.2", {"start": v(438.8, 15) * mm, "end": v(439.8, 15) * mm});
            skLineSegment(sketch, "E27.0.28.3", {"start": v(439.8, -22.5) * mm, "end": v(439.8, 7.5) * mm});
            skLineSegment(sketch, "E27.3.28.3", {"start": v(436.8, 22.5) * mm, "end": v(436.8, -7.5) * mm});
            skPoint(sketch, "E27.6.28.3", {"position": v(436.8, 7.5) * mm});
            skLineSegment(sketch, "E27.7.28.3", {"start": v(437.8, -7.5) * mm, "end": v(437.8, 22.5) * mm});
            skLineSegment(sketch, "E27.10.28.3", {"start": v(438.8, 7.5) * mm, "end": v(438.8, -22.5) * mm});
            skLineSegment(sketch, "E27.13.28.3", {"start": v(436.8, -7.5) * mm, "end": v(437.8, -7.5) * mm});
            skLineSegment(sketch, "E27.16.28.3", {"start": v(439.8, 7.5) * mm, "end": v(438.8, 7.5) * mm});
            skLineSegment(sketch, "E27.19.28.3", {"start": v(437.8, 22.5) * mm, "end": v(436.8, 22.5) * mm});
            skLineSegment(sketch, "E27.22.28.3", {"start": v(438.8, -22.5) * mm, "end": v(439.8, -22.5) * mm});
            skLineSegment(sketch, "E27.0.29.0", {"start": v(443.8, 90) * mm, "end": v(443.8, 120) * mm});
            skLineSegment(sketch, "E27.3.29.0", {"start": v(440.8, 135) * mm, "end": v(440.8, 105) * mm});
            skPoint(sketch, "E27.6.29.0", {"position": v(440.8, 120) * mm});
            skLineSegment(sketch, "E27.7.29.0", {"start": v(441.8, 105) * mm, "end": v(441.8, 135) * mm});
            skLineSegment(sketch, "E27.10.29.0", {"start": v(442.8, 120) * mm, "end": v(442.8, 90) * mm});
            skLineSegment(sketch, "E27.13.29.0", {"start": v(440.8, 105) * mm, "end": v(441.8, 105) * mm});
            skLineSegment(sketch, "E27.16.29.0", {"start": v(443.8, 120) * mm, "end": v(442.8, 120) * mm});
            skLineSegment(sketch, "E27.19.29.0", {"start": v(441.8, 135) * mm, "end": v(440.8, 135) * mm});
            skLineSegment(sketch, "E27.22.29.0", {"start": v(442.8, 90) * mm, "end": v(443.8, 90) * mm});
            skLineSegment(sketch, "E27.0.29.1", {"start": v(443.8, 52.5) * mm, "end": v(443.8, 82.5) * mm});
            skLineSegment(sketch, "E27.3.29.1", {"start": v(440.8, 97.5) * mm, "end": v(440.8, 67.5) * mm});
            skPoint(sketch, "E27.6.29.1", {"position": v(440.8, 82.5) * mm});
            skLineSegment(sketch, "E27.7.29.1", {"start": v(441.8, 67.5) * mm, "end": v(441.8, 97.5) * mm});
            skLineSegment(sketch, "E27.10.29.1", {"start": v(442.8, 82.5) * mm, "end": v(442.8, 52.5) * mm});
            skLineSegment(sketch, "E27.13.29.1", {"start": v(440.8, 67.5) * mm, "end": v(441.8, 67.5) * mm});
            skLineSegment(sketch, "E27.16.29.1", {"start": v(443.8, 82.5) * mm, "end": v(442.8, 82.5) * mm});
            skLineSegment(sketch, "E27.19.29.1", {"start": v(441.8, 97.5) * mm, "end": v(440.8, 97.5) * mm});
            skLineSegment(sketch, "E27.22.29.1", {"start": v(442.8, 52.5) * mm, "end": v(443.8, 52.5) * mm});
            skLineSegment(sketch, "E27.0.29.2", {"start": v(443.8, 15) * mm, "end": v(443.8, 45) * mm});
            skLineSegment(sketch, "E27.3.29.2", {"start": v(440.8, 60) * mm, "end": v(440.8, 30) * mm});
            skPoint(sketch, "E27.6.29.2", {"position": v(440.8, 45) * mm});
            skLineSegment(sketch, "E27.7.29.2", {"start": v(441.8, 30) * mm, "end": v(441.8, 60) * mm});
            skLineSegment(sketch, "E27.10.29.2", {"start": v(442.8, 45) * mm, "end": v(442.8, 15) * mm});
            skLineSegment(sketch, "E27.13.29.2", {"start": v(440.8, 30) * mm, "end": v(441.8, 30) * mm});
            skLineSegment(sketch, "E27.16.29.2", {"start": v(443.8, 45) * mm, "end": v(442.8, 45) * mm});
            skLineSegment(sketch, "E27.19.29.2", {"start": v(441.8, 60) * mm, "end": v(440.8, 60) * mm});
            skLineSegment(sketch, "E27.22.29.2", {"start": v(442.8, 15) * mm, "end": v(443.8, 15) * mm});
            skLineSegment(sketch, "E27.0.29.3", {"start": v(443.8, -22.5) * mm, "end": v(443.8, 7.5) * mm});
            skLineSegment(sketch, "E27.3.29.3", {"start": v(440.8, 22.5) * mm, "end": v(440.8, -7.5) * mm});
            skPoint(sketch, "E27.6.29.3", {"position": v(440.8, 7.5) * mm});
            skLineSegment(sketch, "E27.7.29.3", {"start": v(441.8, -7.5) * mm, "end": v(441.8, 22.5) * mm});
            skLineSegment(sketch, "E27.10.29.3", {"start": v(442.8, 7.5) * mm, "end": v(442.8, -22.5) * mm});
            skLineSegment(sketch, "E27.13.29.3", {"start": v(440.8, -7.5) * mm, "end": v(441.8, -7.5) * mm});
            skLineSegment(sketch, "E27.16.29.3", {"start": v(443.8, 7.5) * mm, "end": v(442.8, 7.5) * mm});
            skLineSegment(sketch, "E27.19.29.3", {"start": v(441.8, 22.5) * mm, "end": v(440.8, 22.5) * mm});
            skLineSegment(sketch, "E27.22.29.3", {"start": v(442.8, -22.5) * mm, "end": v(443.8, -22.5) * mm});
            skLineSegment(sketch, "E28.0.30.0", {"start": v(447.8, 90) * mm, "end": v(447.8, 120) * mm});
            skLineSegment(sketch, "E28.3.30.0", {"start": v(444.8, 135) * mm, "end": v(444.8, 105) * mm});
            skPoint(sketch, "E28.6.30.0", {"position": v(444.8, 120) * mm});
            skLineSegment(sketch, "E28.7.30.0", {"start": v(445.8, 105) * mm, "end": v(445.8, 135) * mm});
            skLineSegment(sketch, "E28.10.30.0", {"start": v(446.8, 120) * mm, "end": v(446.8, 90) * mm});
            skLineSegment(sketch, "E28.13.30.0", {"start": v(444.8, 105) * mm, "end": v(445.8, 105) * mm});
            skLineSegment(sketch, "E28.16.30.0", {"start": v(447.8, 120) * mm, "end": v(446.8, 120) * mm});
            skLineSegment(sketch, "E28.19.30.0", {"start": v(445.8, 135) * mm, "end": v(444.8, 135) * mm});
            skLineSegment(sketch, "E28.22.30.0", {"start": v(446.8, 90) * mm, "end": v(447.8, 90) * mm});
            skLineSegment(sketch, "E28.0.30.1", {"start": v(447.8, 52.5) * mm, "end": v(447.8, 82.5) * mm});
            skLineSegment(sketch, "E28.3.30.1", {"start": v(444.8, 97.5) * mm, "end": v(444.8, 67.5) * mm});
            skPoint(sketch, "E28.6.30.1", {"position": v(444.8, 82.5) * mm});
            skLineSegment(sketch, "E28.7.30.1", {"start": v(445.8, 67.5) * mm, "end": v(445.8, 97.5) * mm});
            skLineSegment(sketch, "E28.10.30.1", {"start": v(446.8, 82.5) * mm, "end": v(446.8, 52.5) * mm});
            skLineSegment(sketch, "E28.13.30.1", {"start": v(444.8, 67.5) * mm, "end": v(445.8, 67.5) * mm});
            skLineSegment(sketch, "E28.16.30.1", {"start": v(447.8, 82.5) * mm, "end": v(446.8, 82.5) * mm});
            skLineSegment(sketch, "E28.19.30.1", {"start": v(445.8, 97.5) * mm, "end": v(444.8, 97.5) * mm});
            skLineSegment(sketch, "E28.22.30.1", {"start": v(446.8, 52.5) * mm, "end": v(447.8, 52.5) * mm});
            skLineSegment(sketch, "E28.0.30.2", {"start": v(447.8, 15) * mm, "end": v(447.8, 45) * mm});
            skLineSegment(sketch, "E28.3.30.2", {"start": v(444.8, 60) * mm, "end": v(444.8, 30) * mm});
            skPoint(sketch, "E28.6.30.2", {"position": v(444.8, 45) * mm});
            skLineSegment(sketch, "E28.7.30.2", {"start": v(445.8, 30) * mm, "end": v(445.8, 60) * mm});
            skLineSegment(sketch, "E28.10.30.2", {"start": v(446.8, 45) * mm, "end": v(446.8, 15) * mm});
            skLineSegment(sketch, "E28.13.30.2", {"start": v(444.8, 30) * mm, "end": v(445.8, 30) * mm});
            skLineSegment(sketch, "E28.16.30.2", {"start": v(447.8, 45) * mm, "end": v(446.8, 45) * mm});
            skLineSegment(sketch, "E28.19.30.2", {"start": v(445.8, 60) * mm, "end": v(444.8, 60) * mm});
            skLineSegment(sketch, "E28.22.30.2", {"start": v(446.8, 15) * mm, "end": v(447.8, 15) * mm});
            skLineSegment(sketch, "E28.0.30.3", {"start": v(447.8, -22.5) * mm, "end": v(447.8, 7.5) * mm});
            skLineSegment(sketch, "E28.3.30.3", {"start": v(444.8, 22.5) * mm, "end": v(444.8, -7.5) * mm});
            skPoint(sketch, "E28.6.30.3", {"position": v(444.8, 7.5) * mm});
            skLineSegment(sketch, "E28.7.30.3", {"start": v(445.8, -7.5) * mm, "end": v(445.8, 22.5) * mm});
            skLineSegment(sketch, "E28.10.30.3", {"start": v(446.8, 7.5) * mm, "end": v(446.8, -22.5) * mm});
            skLineSegment(sketch, "E28.13.30.3", {"start": v(444.8, -7.5) * mm, "end": v(445.8, -7.5) * mm});
            skLineSegment(sketch, "E28.16.30.3", {"start": v(447.8, 7.5) * mm, "end": v(446.8, 7.5) * mm});
            skLineSegment(sketch, "E28.19.30.3", {"start": v(445.8, 22.5) * mm, "end": v(444.8, 22.5) * mm});
            skLineSegment(sketch, "E28.22.30.3", {"start": v(446.8, -22.5) * mm, "end": v(447.8, -22.5) * mm});
            skLineSegment(sketch, "E28.0.31.0", {"start": v(451.8, 90) * mm, "end": v(451.8, 120) * mm});
            skLineSegment(sketch, "E28.3.31.0", {"start": v(448.8, 135) * mm, "end": v(448.8, 105) * mm});
            skPoint(sketch, "E28.6.31.0", {"position": v(448.8, 120) * mm});
            skLineSegment(sketch, "E28.7.31.0", {"start": v(449.8, 105) * mm, "end": v(449.8, 135) * mm});
            skLineSegment(sketch, "E28.10.31.0", {"start": v(450.8, 120) * mm, "end": v(450.8, 90) * mm});
            skLineSegment(sketch, "E28.13.31.0", {"start": v(448.8, 105) * mm, "end": v(449.8, 105) * mm});
            skLineSegment(sketch, "E28.16.31.0", {"start": v(451.8, 120) * mm, "end": v(450.8, 120) * mm});
            skLineSegment(sketch, "E28.19.31.0", {"start": v(449.8, 135) * mm, "end": v(448.8, 135) * mm});
            skLineSegment(sketch, "E28.22.31.0", {"start": v(450.8, 90) * mm, "end": v(451.8, 90) * mm});
            skLineSegment(sketch, "E28.0.31.1", {"start": v(451.8, 52.5) * mm, "end": v(451.8, 82.5) * mm});
            skLineSegment(sketch, "E28.3.31.1", {"start": v(448.8, 97.5) * mm, "end": v(448.8, 67.5) * mm});
            skPoint(sketch, "E28.6.31.1", {"position": v(448.8, 82.5) * mm});
            skLineSegment(sketch, "E28.7.31.1", {"start": v(449.8, 67.5) * mm, "end": v(449.8, 97.5) * mm});
            skLineSegment(sketch, "E28.10.31.1", {"start": v(450.8, 82.5) * mm, "end": v(450.8, 52.5) * mm});
            skLineSegment(sketch, "E28.13.31.1", {"start": v(448.8, 67.5) * mm, "end": v(449.8, 67.5) * mm});
            skLineSegment(sketch, "E28.16.31.1", {"start": v(451.8, 82.5) * mm, "end": v(450.8, 82.5) * mm});
            skLineSegment(sketch, "E28.19.31.1", {"start": v(449.8, 97.5) * mm, "end": v(448.8, 97.5) * mm});
            skLineSegment(sketch, "E28.22.31.1", {"start": v(450.8, 52.5) * mm, "end": v(451.8, 52.5) * mm});
            skLineSegment(sketch, "E28.0.31.2", {"start": v(451.8, 15) * mm, "end": v(451.8, 45) * mm});
            skLineSegment(sketch, "E28.3.31.2", {"start": v(448.8, 60) * mm, "end": v(448.8, 30) * mm});
            skPoint(sketch, "E28.6.31.2", {"position": v(448.8, 45) * mm});
            skLineSegment(sketch, "E28.7.31.2", {"start": v(449.8, 30) * mm, "end": v(449.8, 60) * mm});
            skLineSegment(sketch, "E28.10.31.2", {"start": v(450.8, 45) * mm, "end": v(450.8, 15) * mm});
            skLineSegment(sketch, "E28.13.31.2", {"start": v(448.8, 30) * mm, "end": v(449.8, 30) * mm});
            skLineSegment(sketch, "E28.16.31.2", {"start": v(451.8, 45) * mm, "end": v(450.8, 45) * mm});
            skLineSegment(sketch, "E28.19.31.2", {"start": v(449.8, 60) * mm, "end": v(448.8, 60) * mm});
            skLineSegment(sketch, "E28.22.31.2", {"start": v(450.8, 15) * mm, "end": v(451.8, 15) * mm});
            skLineSegment(sketch, "E28.0.31.3", {"start": v(451.8, -22.5) * mm, "end": v(451.8, 7.5) * mm});
            skLineSegment(sketch, "E28.3.31.3", {"start": v(448.8, 22.5) * mm, "end": v(448.8, -7.5) * mm});
            skPoint(sketch, "E28.6.31.3", {"position": v(448.8, 7.5) * mm});
            skLineSegment(sketch, "E28.7.31.3", {"start": v(449.8, -7.5) * mm, "end": v(449.8, 22.5) * mm});
            skLineSegment(sketch, "E28.10.31.3", {"start": v(450.8, 7.5) * mm, "end": v(450.8, -22.5) * mm});
            skLineSegment(sketch, "E28.13.31.3", {"start": v(448.8, -7.5) * mm, "end": v(449.8, -7.5) * mm});
            skLineSegment(sketch, "E28.16.31.3", {"start": v(451.8, 7.5) * mm, "end": v(450.8, 7.5) * mm});
            skLineSegment(sketch, "E28.19.31.3", {"start": v(449.8, 22.5) * mm, "end": v(448.8, 22.5) * mm});
            skLineSegment(sketch, "E28.22.31.3", {"start": v(450.8, -22.5) * mm, "end": v(451.8, -22.5) * mm});
            skLineSegment(sketch, "E28.0.32.0", {"start": v(455.8, 90) * mm, "end": v(455.8, 120) * mm});
            skLineSegment(sketch, "E28.3.32.0", {"start": v(452.8, 135) * mm, "end": v(452.8, 105) * mm});
            skPoint(sketch, "E28.6.32.0", {"position": v(452.8, 120) * mm});
            skLineSegment(sketch, "E28.7.32.0", {"start": v(453.8, 105) * mm, "end": v(453.8, 135) * mm});
            skLineSegment(sketch, "E28.10.32.0", {"start": v(454.8, 120) * mm, "end": v(454.8, 90) * mm});
            skLineSegment(sketch, "E28.13.32.0", {"start": v(452.8, 105) * mm, "end": v(453.8, 105) * mm});
            skLineSegment(sketch, "E28.16.32.0", {"start": v(455.8, 120) * mm, "end": v(454.8, 120) * mm});
            skLineSegment(sketch, "E28.19.32.0", {"start": v(453.8, 135) * mm, "end": v(452.8, 135) * mm});
            skLineSegment(sketch, "E28.22.32.0", {"start": v(454.8, 90) * mm, "end": v(455.8, 90) * mm});
            skLineSegment(sketch, "E28.0.32.1", {"start": v(455.8, 52.5) * mm, "end": v(455.8, 82.5) * mm});
            skLineSegment(sketch, "E28.3.32.1", {"start": v(452.8, 97.5) * mm, "end": v(452.8, 67.5) * mm});
            skPoint(sketch, "E28.6.32.1", {"position": v(452.8, 82.5) * mm});
            skLineSegment(sketch, "E28.7.32.1", {"start": v(453.8, 67.5) * mm, "end": v(453.8, 97.5) * mm});
            skLineSegment(sketch, "E28.10.32.1", {"start": v(454.8, 82.5) * mm, "end": v(454.8, 52.5) * mm});
            skLineSegment(sketch, "E28.13.32.1", {"start": v(452.8, 67.5) * mm, "end": v(453.8, 67.5) * mm});
            skLineSegment(sketch, "E28.16.32.1", {"start": v(455.8, 82.5) * mm, "end": v(454.8, 82.5) * mm});
            skLineSegment(sketch, "E28.19.32.1", {"start": v(453.8, 97.5) * mm, "end": v(452.8, 97.5) * mm});
            skLineSegment(sketch, "E28.22.32.1", {"start": v(454.8, 52.5) * mm, "end": v(455.8, 52.5) * mm});
            skLineSegment(sketch, "E28.0.32.2", {"start": v(455.8, 15) * mm, "end": v(455.8, 45) * mm});
            skLineSegment(sketch, "E28.3.32.2", {"start": v(452.8, 60) * mm, "end": v(452.8, 30) * mm});
            skPoint(sketch, "E28.6.32.2", {"position": v(452.8, 45) * mm});
            skLineSegment(sketch, "E28.7.32.2", {"start": v(453.8, 30) * mm, "end": v(453.8, 60) * mm});
            skLineSegment(sketch, "E28.10.32.2", {"start": v(454.8, 45) * mm, "end": v(454.8, 15) * mm});
            skLineSegment(sketch, "E28.13.32.2", {"start": v(452.8, 30) * mm, "end": v(453.8, 30) * mm});
            skLineSegment(sketch, "E28.16.32.2", {"start": v(455.8, 45) * mm, "end": v(454.8, 45) * mm});
            skLineSegment(sketch, "E28.19.32.2", {"start": v(453.8, 60) * mm, "end": v(452.8, 60) * mm});
            skLineSegment(sketch, "E28.22.32.2", {"start": v(454.8, 15) * mm, "end": v(455.8, 15) * mm});
            skLineSegment(sketch, "E28.0.32.3", {"start": v(455.8, -22.5) * mm, "end": v(455.8, 7.5) * mm});
            skLineSegment(sketch, "E28.3.32.3", {"start": v(452.8, 22.5) * mm, "end": v(452.8, -7.5) * mm});
            skPoint(sketch, "E28.6.32.3", {"position": v(452.8, 7.5) * mm});
            skLineSegment(sketch, "E28.7.32.3", {"start": v(453.8, -7.5) * mm, "end": v(453.8, 22.5) * mm});
            skLineSegment(sketch, "E28.10.32.3", {"start": v(454.8, 7.5) * mm, "end": v(454.8, -22.5) * mm});
            skLineSegment(sketch, "E28.13.32.3", {"start": v(452.8, -7.5) * mm, "end": v(453.8, -7.5) * mm});
            skLineSegment(sketch, "E28.16.32.3", {"start": v(455.8, 7.5) * mm, "end": v(454.8, 7.5) * mm});
            skLineSegment(sketch, "E28.19.32.3", {"start": v(453.8, 22.5) * mm, "end": v(452.8, 22.5) * mm});
            skLineSegment(sketch, "E28.22.32.3", {"start": v(454.8, -22.5) * mm, "end": v(455.8, -22.5) * mm});
            skLineSegment(sketch, "E28.0.33.0", {"start": v(459.8, 90) * mm, "end": v(459.8, 120) * mm});
            skLineSegment(sketch, "E28.3.33.0", {"start": v(456.8, 135) * mm, "end": v(456.8, 105) * mm});
            skPoint(sketch, "E28.6.33.0", {"position": v(456.8, 120) * mm});
            skLineSegment(sketch, "E28.7.33.0", {"start": v(457.8, 105) * mm, "end": v(457.8, 135) * mm});
            skLineSegment(sketch, "E28.10.33.0", {"start": v(458.8, 120) * mm, "end": v(458.8, 90) * mm});
            skLineSegment(sketch, "E28.13.33.0", {"start": v(456.8, 105) * mm, "end": v(457.8, 105) * mm});
            skLineSegment(sketch, "E28.16.33.0", {"start": v(459.8, 120) * mm, "end": v(458.8, 120) * mm});
            skLineSegment(sketch, "E28.19.33.0", {"start": v(457.8, 135) * mm, "end": v(456.8, 135) * mm});
            skLineSegment(sketch, "E28.22.33.0", {"start": v(458.8, 90) * mm, "end": v(459.8, 90) * mm});
            skLineSegment(sketch, "E28.0.33.1", {"start": v(459.8, 52.5) * mm, "end": v(459.8, 82.5) * mm});
            skLineSegment(sketch, "E28.3.33.1", {"start": v(456.8, 97.5) * mm, "end": v(456.8, 67.5) * mm});
            skPoint(sketch, "E28.6.33.1", {"position": v(456.8, 82.5) * mm});
            skLineSegment(sketch, "E28.7.33.1", {"start": v(457.8, 67.5) * mm, "end": v(457.8, 97.5) * mm});
            skLineSegment(sketch, "E28.10.33.1", {"start": v(458.8, 82.5) * mm, "end": v(458.8, 52.5) * mm});
            skLineSegment(sketch, "E28.13.33.1", {"start": v(456.8, 67.5) * mm, "end": v(457.8, 67.5) * mm});
            skLineSegment(sketch, "E28.16.33.1", {"start": v(459.8, 82.5) * mm, "end": v(458.8, 82.5) * mm});
            skLineSegment(sketch, "E28.19.33.1", {"start": v(457.8, 97.5) * mm, "end": v(456.8, 97.5) * mm});
            skLineSegment(sketch, "E28.22.33.1", {"start": v(458.8, 52.5) * mm, "end": v(459.8, 52.5) * mm});
            skLineSegment(sketch, "E28.0.33.2", {"start": v(459.8, 15) * mm, "end": v(459.8, 45) * mm});
            skLineSegment(sketch, "E28.3.33.2", {"start": v(456.8, 60) * mm, "end": v(456.8, 30) * mm});
            skPoint(sketch, "E28.6.33.2", {"position": v(456.8, 45) * mm});
            skLineSegment(sketch, "E28.7.33.2", {"start": v(457.8, 30) * mm, "end": v(457.8, 60) * mm});
            skLineSegment(sketch, "E28.10.33.2", {"start": v(458.8, 45) * mm, "end": v(458.8, 15) * mm});
            skLineSegment(sketch, "E28.13.33.2", {"start": v(456.8, 30) * mm, "end": v(457.8, 30) * mm});
            skLineSegment(sketch, "E28.16.33.2", {"start": v(459.8, 45) * mm, "end": v(458.8, 45) * mm});
            skLineSegment(sketch, "E28.19.33.2", {"start": v(457.8, 60) * mm, "end": v(456.8, 60) * mm});
            skLineSegment(sketch, "E28.22.33.2", {"start": v(458.8, 15) * mm, "end": v(459.8, 15) * mm});
            skLineSegment(sketch, "E28.0.33.3", {"start": v(459.8, -22.5) * mm, "end": v(459.8, 7.5) * mm});
            skLineSegment(sketch, "E28.3.33.3", {"start": v(456.8, 22.5) * mm, "end": v(456.8, -7.5) * mm});
            skPoint(sketch, "E28.6.33.3", {"position": v(456.8, 7.5) * mm});
            skLineSegment(sketch, "E28.7.33.3", {"start": v(457.8, -7.5) * mm, "end": v(457.8, 22.5) * mm});
            skLineSegment(sketch, "E28.10.33.3", {"start": v(458.8, 7.5) * mm, "end": v(458.8, -22.5) * mm});
            skLineSegment(sketch, "E28.13.33.3", {"start": v(456.8, -7.5) * mm, "end": v(457.8, -7.5) * mm});
            skLineSegment(sketch, "E28.16.33.3", {"start": v(459.8, 7.5) * mm, "end": v(458.8, 7.5) * mm});
            skLineSegment(sketch, "E28.19.33.3", {"start": v(457.8, 22.5) * mm, "end": v(456.8, 22.5) * mm});
            skLineSegment(sketch, "E28.22.33.3", {"start": v(458.8, -22.5) * mm, "end": v(459.8, -22.5) * mm});
            skLineSegment(sketch, "E28.0.34.0", {"start": v(463.8, 90) * mm, "end": v(463.8, 120) * mm});
            skLineSegment(sketch, "E28.3.34.0", {"start": v(460.8, 135) * mm, "end": v(460.8, 105) * mm});
            skPoint(sketch, "E28.6.34.0", {"position": v(460.8, 120) * mm});
            skLineSegment(sketch, "E28.7.34.0", {"start": v(461.8, 105) * mm, "end": v(461.8, 135) * mm});
            skLineSegment(sketch, "E28.10.34.0", {"start": v(462.8, 120) * mm, "end": v(462.8, 90) * mm});
            skLineSegment(sketch, "E28.13.34.0", {"start": v(460.8, 105) * mm, "end": v(461.8, 105) * mm});
            skLineSegment(sketch, "E28.16.34.0", {"start": v(463.8, 120) * mm, "end": v(462.8, 120) * mm});
            skLineSegment(sketch, "E28.19.34.0", {"start": v(461.8, 135) * mm, "end": v(460.8, 135) * mm});
            skLineSegment(sketch, "E28.22.34.0", {"start": v(462.8, 90) * mm, "end": v(463.8, 90) * mm});
            skLineSegment(sketch, "E28.0.34.1", {"start": v(463.8, 52.5) * mm, "end": v(463.8, 82.5) * mm});
            skLineSegment(sketch, "E28.3.34.1", {"start": v(460.8, 97.5) * mm, "end": v(460.8, 67.5) * mm});
            skPoint(sketch, "E28.6.34.1", {"position": v(460.8, 82.5) * mm});
            skLineSegment(sketch, "E28.7.34.1", {"start": v(461.8, 67.5) * mm, "end": v(461.8, 97.5) * mm});
            skLineSegment(sketch, "E28.10.34.1", {"start": v(462.8, 82.5) * mm, "end": v(462.8, 52.5) * mm});
            skLineSegment(sketch, "E28.13.34.1", {"start": v(460.8, 67.5) * mm, "end": v(461.8, 67.5) * mm});
            skLineSegment(sketch, "E28.16.34.1", {"start": v(463.8, 82.5) * mm, "end": v(462.8, 82.5) * mm});
            skLineSegment(sketch, "E28.19.34.1", {"start": v(461.8, 97.5) * mm, "end": v(460.8, 97.5) * mm});
            skLineSegment(sketch, "E28.22.34.1", {"start": v(462.8, 52.5) * mm, "end": v(463.8, 52.5) * mm});
            skLineSegment(sketch, "E28.0.34.2", {"start": v(463.8, 15) * mm, "end": v(463.8, 45) * mm});
            skLineSegment(sketch, "E28.3.34.2", {"start": v(460.8, 60) * mm, "end": v(460.8, 30) * mm});
            skPoint(sketch, "E28.6.34.2", {"position": v(460.8, 45) * mm});
            skLineSegment(sketch, "E28.7.34.2", {"start": v(461.8, 30) * mm, "end": v(461.8, 60) * mm});
            skLineSegment(sketch, "E28.10.34.2", {"start": v(462.8, 45) * mm, "end": v(462.8, 15) * mm});
            skLineSegment(sketch, "E28.13.34.2", {"start": v(460.8, 30) * mm, "end": v(461.8, 30) * mm});
            skLineSegment(sketch, "E28.16.34.2", {"start": v(463.8, 45) * mm, "end": v(462.8, 45) * mm});
            skLineSegment(sketch, "E28.19.34.2", {"start": v(461.8, 60) * mm, "end": v(460.8, 60) * mm});
            skLineSegment(sketch, "E28.22.34.2", {"start": v(462.8, 15) * mm, "end": v(463.8, 15) * mm});
            skLineSegment(sketch, "E28.0.34.3", {"start": v(463.8, -22.5) * mm, "end": v(463.8, 7.5) * mm});
            skLineSegment(sketch, "E28.3.34.3", {"start": v(460.8, 22.5) * mm, "end": v(460.8, -7.5) * mm});
            skPoint(sketch, "E28.6.34.3", {"position": v(460.8, 7.5) * mm});
            skLineSegment(sketch, "E28.7.34.3", {"start": v(461.8, -7.5) * mm, "end": v(461.8, 22.5) * mm});
            skLineSegment(sketch, "E28.10.34.3", {"start": v(462.8, 7.5) * mm, "end": v(462.8, -22.5) * mm});
            skLineSegment(sketch, "E28.13.34.3", {"start": v(460.8, -7.5) * mm, "end": v(461.8, -7.5) * mm});
            skLineSegment(sketch, "E28.16.34.3", {"start": v(463.8, 7.5) * mm, "end": v(462.8, 7.5) * mm});
            skLineSegment(sketch, "E28.19.34.3", {"start": v(461.8, 22.5) * mm, "end": v(460.8, 22.5) * mm});
            skLineSegment(sketch, "E28.22.34.3", {"start": v(462.8, -22.5) * mm, "end": v(463.8, -22.5) * mm});
            skLineSegment(sketch, "E29.0.35.0", {"start": v(467.8, 90) * mm, "end": v(467.8, 120) * mm});
            skLineSegment(sketch, "E29.3.35.0", {"start": v(464.8, 135) * mm, "end": v(464.8, 105) * mm});
            skPoint(sketch, "E29.6.35.0", {"position": v(464.8, 120) * mm});
            skLineSegment(sketch, "E29.7.35.0", {"start": v(465.8, 105) * mm, "end": v(465.8, 135) * mm});
            skLineSegment(sketch, "E29.10.35.0", {"start": v(466.8, 120) * mm, "end": v(466.8, 90) * mm});
            skLineSegment(sketch, "E29.13.35.0", {"start": v(464.8, 105) * mm, "end": v(465.8, 105) * mm});
            skLineSegment(sketch, "E29.16.35.0", {"start": v(467.8, 120) * mm, "end": v(466.8, 120) * mm});
            skLineSegment(sketch, "E29.19.35.0", {"start": v(465.8, 135) * mm, "end": v(464.8, 135) * mm});
            skLineSegment(sketch, "E29.22.35.0", {"start": v(466.8, 90) * mm, "end": v(467.8, 90) * mm});
            skLineSegment(sketch, "E29.0.35.1", {"start": v(467.8, 52.5) * mm, "end": v(467.8, 82.5) * mm});
            skLineSegment(sketch, "E29.3.35.1", {"start": v(464.8, 97.5) * mm, "end": v(464.8, 67.5) * mm});
            skPoint(sketch, "E29.6.35.1", {"position": v(464.8, 82.5) * mm});
            skLineSegment(sketch, "E29.7.35.1", {"start": v(465.8, 67.5) * mm, "end": v(465.8, 97.5) * mm});
            skLineSegment(sketch, "E29.10.35.1", {"start": v(466.8, 82.5) * mm, "end": v(466.8, 52.5) * mm});
            skLineSegment(sketch, "E29.13.35.1", {"start": v(464.8, 67.5) * mm, "end": v(465.8, 67.5) * mm});
            skLineSegment(sketch, "E29.16.35.1", {"start": v(467.8, 82.5) * mm, "end": v(466.8, 82.5) * mm});
            skLineSegment(sketch, "E29.19.35.1", {"start": v(465.8, 97.5) * mm, "end": v(464.8, 97.5) * mm});
            skLineSegment(sketch, "E29.22.35.1", {"start": v(466.8, 52.5) * mm, "end": v(467.8, 52.5) * mm});
            skLineSegment(sketch, "E29.0.35.2", {"start": v(467.8, 15) * mm, "end": v(467.8, 45) * mm});
            skLineSegment(sketch, "E29.3.35.2", {"start": v(464.8, 60) * mm, "end": v(464.8, 30) * mm});
            skPoint(sketch, "E29.6.35.2", {"position": v(464.8, 45) * mm});
            skLineSegment(sketch, "E29.7.35.2", {"start": v(465.8, 30) * mm, "end": v(465.8, 60) * mm});
            skLineSegment(sketch, "E29.10.35.2", {"start": v(466.8, 45) * mm, "end": v(466.8, 15) * mm});
            skLineSegment(sketch, "E29.13.35.2", {"start": v(464.8, 30) * mm, "end": v(465.8, 30) * mm});
            skLineSegment(sketch, "E29.16.35.2", {"start": v(467.8, 45) * mm, "end": v(466.8, 45) * mm});
            skLineSegment(sketch, "E29.19.35.2", {"start": v(465.8, 60) * mm, "end": v(464.8, 60) * mm});
            skLineSegment(sketch, "E29.22.35.2", {"start": v(466.8, 15) * mm, "end": v(467.8, 15) * mm});
            skLineSegment(sketch, "E29.0.35.3", {"start": v(467.8, -22.5) * mm, "end": v(467.8, 7.5) * mm});
            skLineSegment(sketch, "E29.3.35.3", {"start": v(464.8, 22.5) * mm, "end": v(464.8, -7.5) * mm});
            skPoint(sketch, "E29.6.35.3", {"position": v(464.8, 7.5) * mm});
            skLineSegment(sketch, "E29.7.35.3", {"start": v(465.8, -7.5) * mm, "end": v(465.8, 22.5) * mm});
            skLineSegment(sketch, "E29.10.35.3", {"start": v(466.8, 7.5) * mm, "end": v(466.8, -22.5) * mm});
            skLineSegment(sketch, "E29.13.35.3", {"start": v(464.8, -7.5) * mm, "end": v(465.8, -7.5) * mm});
            skLineSegment(sketch, "E29.16.35.3", {"start": v(467.8, 7.5) * mm, "end": v(466.8, 7.5) * mm});
            skLineSegment(sketch, "E29.19.35.3", {"start": v(465.8, 22.5) * mm, "end": v(464.8, 22.5) * mm});
            skLineSegment(sketch, "E29.22.35.3", {"start": v(466.8, -22.5) * mm, "end": v(467.8, -22.5) * mm});
            const initialGuessF0  = {"E7": [0.01562, 0.03, 1, 0, 0.06]};
            skSetInitialGuess(sketch, initialGuessF0);
            skSolve(sketch);
        }
        {
            assignVariable(context, id + "F1", {"name" : "MaterialThickness", "anyValue" : 4.5});
        }
        {
            var Q0;
            {var subQ121=sQuery(id+"F0.wireOp",EDGE,"E1");Q0=makeQuery(id+"F0.imprint","IMPRINT",FACE,{"disambiguationData":[TD([[makeQuery(id+"F0.imprint","IMPRINT",EDGE,{"derivedFrom":subQ121}),1.0]])]});}
            extrude(context, id + "F2", {"entities" : qUnion([Q0]), "depth" : (getVariable(context, 'MaterialThickness')) * mm});
        }
    });
